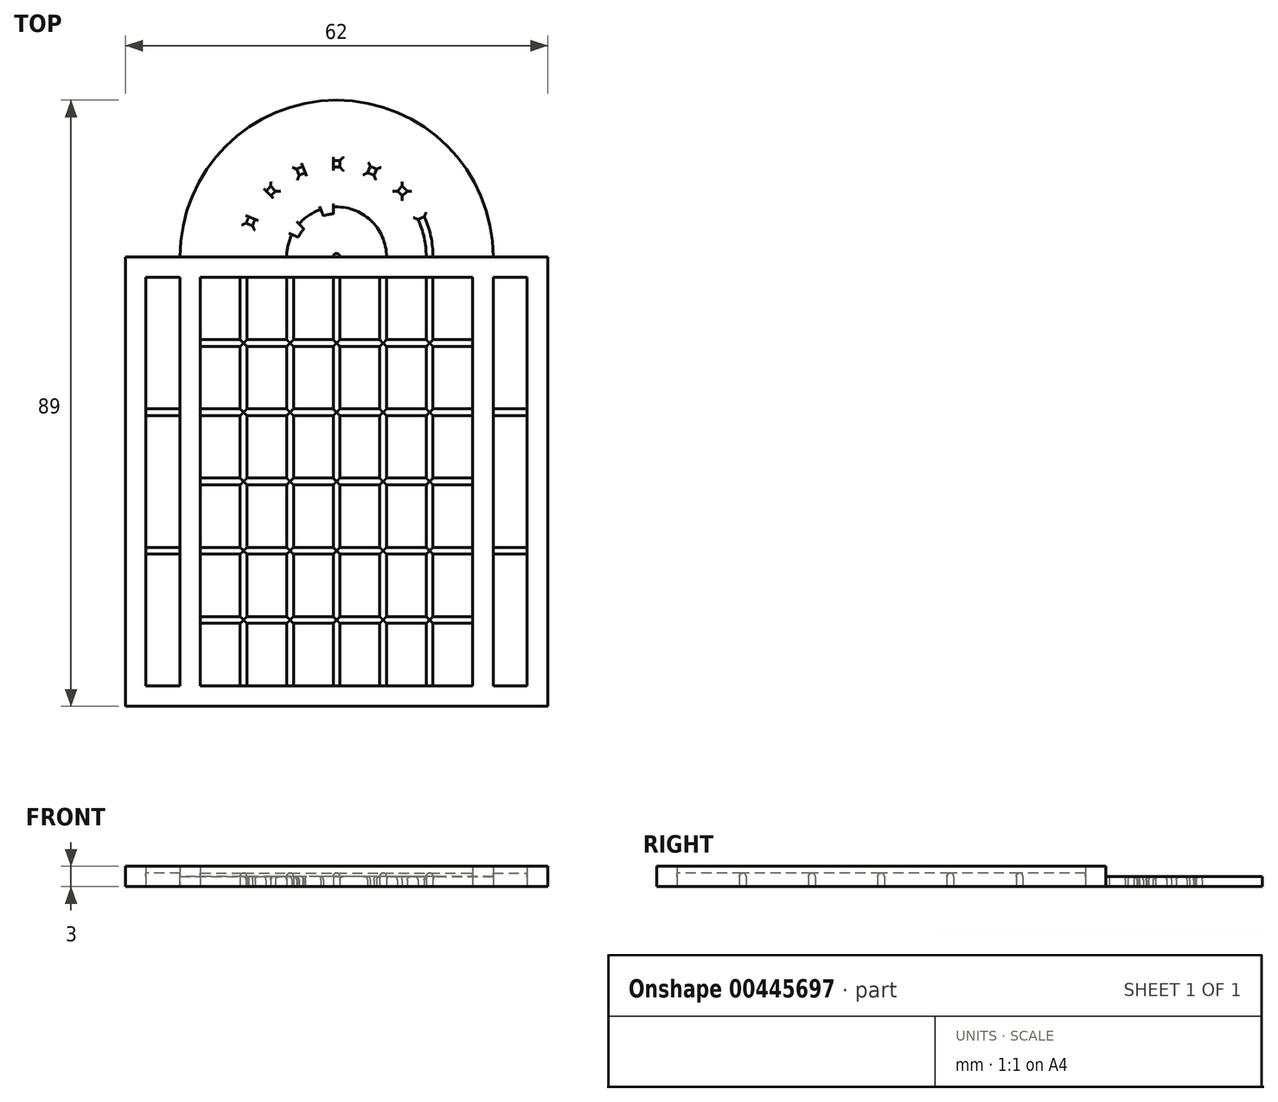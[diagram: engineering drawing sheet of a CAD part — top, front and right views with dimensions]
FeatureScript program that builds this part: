
annotation { "Feature Type Name" : "Feature", "Feature Type Description" : "" }
export const myFeature = defineFeature(function(context is Context, id is Id, definition is map)
    precondition{}
    {
        {
            var Q0;
            Q0=qCreatedBy(makeId("Top.planeOp"),FACE);
            var sketch = newSketch(context, id + "F0", { "sketchPlane" : qUnion([Q0])});
            skLineSegment(sketch, "E0.bottom", {"start": v(0, 0) * mm, "end": v(62, 0) * mm});
            skLineSegment(sketch, "E0.top", {"start": v(0, 60) * mm, "end": v(62, 60) * mm});
            skLineSegment(sketch, "E0.left", {"start": v(0, 0) * mm, "end": v(0, 60) * mm});
            skLineSegment(sketch, "E0.right", {"start": v(62, 0) * mm, "end": v(62, 60) * mm});
            skLineSegment(sketch, "E1", {"start": v(0, 0) * mm, "end": v(8, 0) * mm, "construction": true});
            skLineSegment(sketch, "E2", {"start": v(62, 0) * mm, "end": v(54, 0) * mm, "construction": true});
            skLineSegment(sketch, "E3", {"start": v(62, 0) * mm, "end": v(59, 0) * mm, "construction": true});
            skLineSegment(sketch, "E4", {"start": v(59, 0) * mm, "end": v(59, 60) * mm});
            skLineSegment(sketch, "E5", {"start": v(0, 60) * mm, "end": v(3, 60) * mm, "construction": true});
            skLineSegment(sketch, "E6", {"start": v(3, 60) * mm, "end": v(3, 0) * mm});
            skLineSegment(sketch, "E7", {"start": v(8, 0) * mm, "end": v(8, 60) * mm});
            skLineSegment(sketch, "E8", {"start": v(54, 0) * mm, "end": v(54, 60) * mm});
            skLineSegment(sketch, "E9", {"start": v(8, 0) * mm, "end": v(11, 0) * mm, "construction": true});
            skLineSegment(sketch, "E10", {"start": v(54, 0) * mm, "end": v(51, 0) * mm, "construction": true});
            skLineSegment(sketch, "E11", {"start": v(11, 0) * mm, "end": v(11, 60) * mm});
            skLineSegment(sketch, "E12", {"start": v(51, 0) * mm, "end": v(51, 60) * mm});
            skLineSegment(sketch, "E13.bottom", {"start": v(51, 0) * mm, "end": v(45.17, 0) * mm});
            skLineSegment(sketch, "E13.top", {"start": v(51, 9.17) * mm, "end": v(45.17, 9.17) * mm});
            skLineSegment(sketch, "E13.left", {"start": v(51, 0) * mm, "end": v(51, 9.17) * mm});
            skLineSegment(sketch, "E13.right", {"start": v(45.17, 0) * mm, "end": v(45.17, 9.17) * mm});
            skLineSegment(sketch, "E14.bottom", {"start": v(45.17, 0) * mm, "end": v(44.17, 0) * mm});
            skLineSegment(sketch, "E14.top", {"start": v(45.17, 9.17) * mm, "end": v(44.17, 9.17) * mm, "construction": true});
            skLineSegment(sketch, "E14.right", {"start": v(44.17, 0) * mm, "end": v(44.17, 9.17) * mm});
            skLineSegment(sketch, "E15.top", {"start": v(51, 10.17) * mm, "end": v(45.17, 10.17) * mm});
            skLineSegment(sketch, "E15.left", {"start": v(51, 9.17) * mm, "end": v(51, 10.17) * mm});
            skLineSegment(sketch, "E15.right", {"start": v(45.17, 9.17) * mm, "end": v(45.17, 10.17) * mm, "construction": true});
            skLineSegment(sketch, "E16", {"start": v(44.17, 9.17) * mm, "end": v(44.17, 10.17) * mm, "construction": true});
            skLineSegment(sketch, "E17", {"start": v(44.17, 10.17) * mm, "end": v(45.17, 10.17) * mm, "construction": true});
            skLineSegment(sketch, "E18.0.1.0", {"start": v(44.17, 20.33) * mm, "end": v(45.17, 20.33) * mm, "construction": true});
            skLineSegment(sketch, "E18.0.1.1", {"start": v(51, 20.33) * mm, "end": v(45.17, 20.33) * mm});
            skLineSegment(sketch, "E18.0.1.2", {"start": v(51, 19.33) * mm, "end": v(45.17, 19.33) * mm});
            skLineSegment(sketch, "E18.0.1.3", {"start": v(45.17, 10.17) * mm, "end": v(45.17, 19.33) * mm});
            skLineSegment(sketch, "E18.0.1.4", {"start": v(44.17, 10.17) * mm, "end": v(44.17, 19.33) * mm});
            skLineSegment(sketch, "E18.0.1.5", {"start": v(45.17, 19.33) * mm, "end": v(44.17, 19.33) * mm, "construction": true});
            skLineSegment(sketch, "E18.0.1.6", {"start": v(44.17, 19.33) * mm, "end": v(44.17, 20.33) * mm, "construction": true});
            skLineSegment(sketch, "E18.0.1.7", {"start": v(45.17, 19.33) * mm, "end": v(45.17, 20.33) * mm, "construction": true});
            skLineSegment(sketch, "E18.0.2.0", {"start": v(44.17, 30.5) * mm, "end": v(45.17, 30.5) * mm, "construction": true});
            skLineSegment(sketch, "E18.0.2.1", {"start": v(51, 30.5) * mm, "end": v(45.17, 30.5) * mm});
            skLineSegment(sketch, "E18.0.2.2", {"start": v(51, 29.5) * mm, "end": v(45.17, 29.5) * mm});
            skLineSegment(sketch, "E18.0.2.3", {"start": v(45.17, 20.33) * mm, "end": v(45.17, 29.5) * mm});
            skLineSegment(sketch, "E18.0.2.4", {"start": v(44.17, 20.33) * mm, "end": v(44.17, 29.5) * mm});
            skLineSegment(sketch, "E18.0.2.5", {"start": v(45.17, 29.5) * mm, "end": v(44.17, 29.5) * mm, "construction": true});
            skLineSegment(sketch, "E18.0.2.6", {"start": v(44.17, 29.5) * mm, "end": v(44.17, 30.5) * mm, "construction": true});
            skLineSegment(sketch, "E18.0.2.7", {"start": v(45.17, 29.5) * mm, "end": v(45.17, 30.5) * mm, "construction": true});
            skLineSegment(sketch, "E18.0.3.0", {"start": v(44.17, 40.67) * mm, "end": v(45.17, 40.67) * mm, "construction": true});
            skLineSegment(sketch, "E18.0.3.1", {"start": v(51, 40.67) * mm, "end": v(45.17, 40.67) * mm});
            skLineSegment(sketch, "E18.0.3.2", {"start": v(51, 39.67) * mm, "end": v(45.17, 39.67) * mm});
            skLineSegment(sketch, "E18.0.3.3", {"start": v(45.17, 30.5) * mm, "end": v(45.17, 39.67) * mm});
            skLineSegment(sketch, "E18.0.3.4", {"start": v(44.17, 30.5) * mm, "end": v(44.17, 39.67) * mm});
            skLineSegment(sketch, "E18.0.3.5", {"start": v(45.17, 39.67) * mm, "end": v(44.17, 39.67) * mm, "construction": true});
            skLineSegment(sketch, "E18.0.3.6", {"start": v(44.17, 39.67) * mm, "end": v(44.17, 40.67) * mm, "construction": true});
            skLineSegment(sketch, "E18.0.3.7", {"start": v(45.17, 39.67) * mm, "end": v(45.17, 40.67) * mm, "construction": true});
            skLineSegment(sketch, "E18.0.4.0", {"start": v(44.17, 50.83) * mm, "end": v(45.17, 50.83) * mm, "construction": true});
            skLineSegment(sketch, "E18.0.4.1", {"start": v(51, 50.83) * mm, "end": v(45.17, 50.83) * mm});
            skLineSegment(sketch, "E18.0.4.2", {"start": v(51, 49.83) * mm, "end": v(45.17, 49.83) * mm});
            skLineSegment(sketch, "E18.0.4.3", {"start": v(45.17, 40.67) * mm, "end": v(45.17, 49.83) * mm});
            skLineSegment(sketch, "E18.0.4.4", {"start": v(44.17, 40.67) * mm, "end": v(44.17, 49.83) * mm});
            skLineSegment(sketch, "E18.0.4.5", {"start": v(45.17, 49.83) * mm, "end": v(44.17, 49.83) * mm, "construction": true});
            skLineSegment(sketch, "E18.0.4.6", {"start": v(44.17, 49.83) * mm, "end": v(44.17, 50.83) * mm, "construction": true});
            skLineSegment(sketch, "E18.0.4.7", {"start": v(45.17, 49.83) * mm, "end": v(45.17, 50.83) * mm, "construction": true});
            skLineSegment(sketch, "E18.0.5.2", {"start": v(51, 60) * mm, "end": v(45.17, 60) * mm});
            skLineSegment(sketch, "E18.0.5.3", {"start": v(45.17, 50.83) * mm, "end": v(45.17, 60) * mm});
            skLineSegment(sketch, "E18.0.5.4", {"start": v(44.17, 50.83) * mm, "end": v(44.17, 60) * mm});
            skLineSegment(sketch, "E18.0.5.5", {"start": v(45.17, 60) * mm, "end": v(44.17, 60) * mm, "construction": true});
            skLineSegment(sketch, "E18.1.0.0", {"start": v(37.33, 10.17) * mm, "end": v(38.33, 10.17) * mm, "construction": true});
            skLineSegment(sketch, "E18.1.0.1", {"start": v(44.17, 10.17) * mm, "end": v(38.33, 10.17) * mm});
            skLineSegment(sketch, "E18.1.0.2", {"start": v(44.17, 9.17) * mm, "end": v(38.33, 9.17) * mm});
            skLineSegment(sketch, "E18.1.0.3", {"start": v(38.33, 0) * mm, "end": v(38.33, 9.17) * mm});
            skLineSegment(sketch, "E18.1.0.4", {"start": v(37.33, 0) * mm, "end": v(37.33, 9.17) * mm});
            skLineSegment(sketch, "E18.1.0.5", {"start": v(38.33, 9.17) * mm, "end": v(37.33, 9.17) * mm, "construction": true});
            skLineSegment(sketch, "E18.1.0.6", {"start": v(37.33, 9.17) * mm, "end": v(37.33, 10.17) * mm, "construction": true});
            skLineSegment(sketch, "E18.1.0.7", {"start": v(38.33, 9.17) * mm, "end": v(38.33, 10.17) * mm, "construction": true});
            skLineSegment(sketch, "E18.1.1.0", {"start": v(37.33, 20.33) * mm, "end": v(38.33, 20.33) * mm, "construction": true});
            skLineSegment(sketch, "E18.1.1.1", {"start": v(44.17, 20.33) * mm, "end": v(38.33, 20.33) * mm});
            skLineSegment(sketch, "E18.1.1.2", {"start": v(44.17, 19.33) * mm, "end": v(38.33, 19.33) * mm});
            skLineSegment(sketch, "E18.1.1.3", {"start": v(38.33, 10.17) * mm, "end": v(38.33, 19.33) * mm});
            skLineSegment(sketch, "E18.1.1.4", {"start": v(37.33, 10.17) * mm, "end": v(37.33, 19.33) * mm});
            skLineSegment(sketch, "E18.1.1.5", {"start": v(38.33, 19.33) * mm, "end": v(37.33, 19.33) * mm, "construction": true});
            skLineSegment(sketch, "E18.1.1.6", {"start": v(37.33, 19.33) * mm, "end": v(37.33, 20.33) * mm, "construction": true});
            skLineSegment(sketch, "E18.1.1.7", {"start": v(38.33, 19.33) * mm, "end": v(38.33, 20.33) * mm, "construction": true});
            skLineSegment(sketch, "E18.1.2.0", {"start": v(37.33, 30.5) * mm, "end": v(38.33, 30.5) * mm, "construction": true});
            skLineSegment(sketch, "E18.1.2.1", {"start": v(44.17, 30.5) * mm, "end": v(38.33, 30.5) * mm});
            skLineSegment(sketch, "E18.1.2.2", {"start": v(44.17, 29.5) * mm, "end": v(38.33, 29.5) * mm});
            skLineSegment(sketch, "E18.1.2.3", {"start": v(38.33, 20.33) * mm, "end": v(38.33, 29.5) * mm});
            skLineSegment(sketch, "E18.1.2.4", {"start": v(37.33, 20.33) * mm, "end": v(37.33, 29.5) * mm});
            skLineSegment(sketch, "E18.1.2.5", {"start": v(38.33, 29.5) * mm, "end": v(37.33, 29.5) * mm, "construction": true});
            skLineSegment(sketch, "E18.1.2.6", {"start": v(37.33, 29.5) * mm, "end": v(37.33, 30.5) * mm, "construction": true});
            skLineSegment(sketch, "E18.1.2.7", {"start": v(38.33, 29.5) * mm, "end": v(38.33, 30.5) * mm, "construction": true});
            skLineSegment(sketch, "E18.1.3.0", {"start": v(37.33, 40.67) * mm, "end": v(38.33, 40.67) * mm, "construction": true});
            skLineSegment(sketch, "E18.1.3.1", {"start": v(44.17, 40.67) * mm, "end": v(38.33, 40.67) * mm});
            skLineSegment(sketch, "E18.1.3.2", {"start": v(44.17, 39.67) * mm, "end": v(38.33, 39.67) * mm});
            skLineSegment(sketch, "E18.1.3.3", {"start": v(38.33, 30.5) * mm, "end": v(38.33, 39.67) * mm});
            skLineSegment(sketch, "E18.1.3.4", {"start": v(37.33, 30.5) * mm, "end": v(37.33, 39.67) * mm});
            skLineSegment(sketch, "E18.1.3.5", {"start": v(38.33, 39.67) * mm, "end": v(37.33, 39.67) * mm, "construction": true});
            skLineSegment(sketch, "E18.1.3.6", {"start": v(37.33, 39.67) * mm, "end": v(37.33, 40.67) * mm, "construction": true});
            skLineSegment(sketch, "E18.1.3.7", {"start": v(38.33, 39.67) * mm, "end": v(38.33, 40.67) * mm, "construction": true});
            skLineSegment(sketch, "E18.1.4.0", {"start": v(37.33, 50.83) * mm, "end": v(38.33, 50.83) * mm, "construction": true});
            skLineSegment(sketch, "E18.1.4.1", {"start": v(44.17, 50.83) * mm, "end": v(38.33, 50.83) * mm});
            skLineSegment(sketch, "E18.1.4.2", {"start": v(44.17, 49.83) * mm, "end": v(38.33, 49.83) * mm});
            skLineSegment(sketch, "E18.1.4.3", {"start": v(38.33, 40.67) * mm, "end": v(38.33, 49.83) * mm});
            skLineSegment(sketch, "E18.1.4.4", {"start": v(37.33, 40.67) * mm, "end": v(37.33, 49.83) * mm});
            skLineSegment(sketch, "E18.1.4.5", {"start": v(38.33, 49.83) * mm, "end": v(37.33, 49.83) * mm, "construction": true});
            skLineSegment(sketch, "E18.1.4.6", {"start": v(37.33, 49.83) * mm, "end": v(37.33, 50.83) * mm, "construction": true});
            skLineSegment(sketch, "E18.1.4.7", {"start": v(38.33, 49.83) * mm, "end": v(38.33, 50.83) * mm, "construction": true});
            skLineSegment(sketch, "E18.1.5.2", {"start": v(44.17, 60) * mm, "end": v(38.33, 60) * mm});
            skLineSegment(sketch, "E18.1.5.3", {"start": v(38.33, 50.83) * mm, "end": v(38.33, 60) * mm});
            skLineSegment(sketch, "E18.1.5.4", {"start": v(37.33, 50.83) * mm, "end": v(37.33, 60) * mm});
            skLineSegment(sketch, "E18.1.5.5", {"start": v(38.33, 60) * mm, "end": v(37.33, 60) * mm, "construction": true});
            skLineSegment(sketch, "E18.2.0.0", {"start": v(30.5, 10.17) * mm, "end": v(31.5, 10.17) * mm, "construction": true});
            skLineSegment(sketch, "E18.2.0.1", {"start": v(37.33, 10.17) * mm, "end": v(31.5, 10.17) * mm});
            skLineSegment(sketch, "E18.2.0.2", {"start": v(37.33, 9.17) * mm, "end": v(31.5, 9.17) * mm});
            skLineSegment(sketch, "E18.2.0.3", {"start": v(31.5, 0) * mm, "end": v(31.5, 9.17) * mm});
            skLineSegment(sketch, "E18.2.0.4", {"start": v(30.5, 0) * mm, "end": v(30.5, 9.17) * mm});
            skLineSegment(sketch, "E18.2.0.5", {"start": v(31.5, 9.17) * mm, "end": v(30.5, 9.17) * mm, "construction": true});
            skLineSegment(sketch, "E18.2.0.6", {"start": v(30.5, 9.17) * mm, "end": v(30.5, 10.17) * mm, "construction": true});
            skLineSegment(sketch, "E18.2.0.7", {"start": v(31.5, 9.17) * mm, "end": v(31.5, 10.17) * mm, "construction": true});
            skLineSegment(sketch, "E18.2.1.0", {"start": v(30.5, 20.33) * mm, "end": v(31.5, 20.33) * mm, "construction": true});
            skLineSegment(sketch, "E18.2.1.1", {"start": v(37.33, 20.33) * mm, "end": v(31.5, 20.33) * mm});
            skLineSegment(sketch, "E18.2.1.2", {"start": v(37.33, 19.33) * mm, "end": v(31.5, 19.33) * mm});
            skLineSegment(sketch, "E18.2.1.3", {"start": v(31.5, 10.17) * mm, "end": v(31.5, 19.33) * mm});
            skLineSegment(sketch, "E18.2.1.4", {"start": v(30.5, 10.17) * mm, "end": v(30.5, 19.33) * mm});
            skLineSegment(sketch, "E18.2.1.5", {"start": v(31.5, 19.33) * mm, "end": v(30.5, 19.33) * mm, "construction": true});
            skLineSegment(sketch, "E18.2.1.6", {"start": v(30.5, 19.33) * mm, "end": v(30.5, 20.33) * mm, "construction": true});
            skLineSegment(sketch, "E18.2.1.7", {"start": v(31.5, 19.33) * mm, "end": v(31.5, 20.33) * mm, "construction": true});
            skLineSegment(sketch, "E18.2.2.0", {"start": v(30.5, 30.5) * mm, "end": v(31.5, 30.5) * mm, "construction": true});
            skLineSegment(sketch, "E18.2.2.1", {"start": v(37.33, 30.5) * mm, "end": v(31.5, 30.5) * mm});
            skLineSegment(sketch, "E18.2.2.2", {"start": v(37.33, 29.5) * mm, "end": v(31.5, 29.5) * mm});
            skLineSegment(sketch, "E18.2.2.3", {"start": v(31.5, 20.33) * mm, "end": v(31.5, 29.5) * mm});
            skLineSegment(sketch, "E18.2.2.4", {"start": v(30.5, 20.33) * mm, "end": v(30.5, 29.5) * mm});
            skLineSegment(sketch, "E18.2.2.5", {"start": v(31.5, 29.5) * mm, "end": v(30.5, 29.5) * mm, "construction": true});
            skLineSegment(sketch, "E18.2.2.6", {"start": v(30.5, 29.5) * mm, "end": v(30.5, 30.5) * mm, "construction": true});
            skLineSegment(sketch, "E18.2.2.7", {"start": v(31.5, 29.5) * mm, "end": v(31.5, 30.5) * mm, "construction": true});
            skLineSegment(sketch, "E18.2.3.0", {"start": v(30.5, 40.67) * mm, "end": v(31.5, 40.67) * mm, "construction": true});
            skLineSegment(sketch, "E18.2.3.1", {"start": v(37.33, 40.67) * mm, "end": v(31.5, 40.67) * mm});
            skLineSegment(sketch, "E18.2.3.2", {"start": v(37.33, 39.67) * mm, "end": v(31.5, 39.67) * mm});
            skLineSegment(sketch, "E18.2.3.3", {"start": v(31.5, 30.5) * mm, "end": v(31.5, 39.67) * mm});
            skLineSegment(sketch, "E18.2.3.4", {"start": v(30.5, 30.5) * mm, "end": v(30.5, 39.67) * mm});
            skLineSegment(sketch, "E18.2.3.5", {"start": v(31.5, 39.67) * mm, "end": v(30.5, 39.67) * mm, "construction": true});
            skLineSegment(sketch, "E18.2.3.6", {"start": v(30.5, 39.67) * mm, "end": v(30.5, 40.67) * mm, "construction": true});
            skLineSegment(sketch, "E18.2.3.7", {"start": v(31.5, 39.67) * mm, "end": v(31.5, 40.67) * mm, "construction": true});
            skLineSegment(sketch, "E18.2.4.0", {"start": v(30.5, 50.83) * mm, "end": v(31.5, 50.83) * mm, "construction": true});
            skLineSegment(sketch, "E18.2.4.1", {"start": v(37.33, 50.83) * mm, "end": v(31.5, 50.83) * mm});
            skLineSegment(sketch, "E18.2.4.2", {"start": v(37.33, 49.83) * mm, "end": v(31.5, 49.83) * mm});
            skLineSegment(sketch, "E18.2.4.3", {"start": v(31.5, 40.67) * mm, "end": v(31.5, 49.83) * mm});
            skLineSegment(sketch, "E18.2.4.4", {"start": v(30.5, 40.67) * mm, "end": v(30.5, 49.83) * mm});
            skLineSegment(sketch, "E18.2.4.5", {"start": v(31.5, 49.83) * mm, "end": v(30.5, 49.83) * mm, "construction": true});
            skLineSegment(sketch, "E18.2.4.6", {"start": v(30.5, 49.83) * mm, "end": v(30.5, 50.83) * mm, "construction": true});
            skLineSegment(sketch, "E18.2.4.7", {"start": v(31.5, 49.83) * mm, "end": v(31.5, 50.83) * mm, "construction": true});
            skLineSegment(sketch, "E18.2.5.2", {"start": v(37.33, 60) * mm, "end": v(31.5, 60) * mm});
            skLineSegment(sketch, "E18.2.5.3", {"start": v(31.5, 50.83) * mm, "end": v(31.5, 60) * mm});
            skLineSegment(sketch, "E18.2.5.4", {"start": v(30.5, 50.83) * mm, "end": v(30.5, 60) * mm});
            skLineSegment(sketch, "E18.2.5.5", {"start": v(31.5, 60) * mm, "end": v(30.5, 60) * mm, "construction": true});
            skLineSegment(sketch, "E18.3.0.0", {"start": v(23.67, 10.17) * mm, "end": v(24.67, 10.17) * mm, "construction": true});
            skLineSegment(sketch, "E18.3.0.1", {"start": v(30.5, 10.17) * mm, "end": v(24.67, 10.17) * mm});
            skLineSegment(sketch, "E18.3.0.2", {"start": v(30.5, 9.17) * mm, "end": v(24.67, 9.17) * mm});
            skLineSegment(sketch, "E18.3.0.3", {"start": v(24.67, 0) * mm, "end": v(24.67, 9.17) * mm});
            skLineSegment(sketch, "E18.3.0.4", {"start": v(23.67, 0) * mm, "end": v(23.67, 9.17) * mm});
            skLineSegment(sketch, "E18.3.0.5", {"start": v(24.67, 9.17) * mm, "end": v(23.67, 9.17) * mm, "construction": true});
            skLineSegment(sketch, "E18.3.0.6", {"start": v(23.67, 9.17) * mm, "end": v(23.67, 10.17) * mm, "construction": true});
            skLineSegment(sketch, "E18.3.0.7", {"start": v(24.67, 9.17) * mm, "end": v(24.67, 10.17) * mm, "construction": true});
            skLineSegment(sketch, "E18.3.1.0", {"start": v(23.67, 20.33) * mm, "end": v(24.67, 20.33) * mm, "construction": true});
            skLineSegment(sketch, "E18.3.1.1", {"start": v(30.5, 20.33) * mm, "end": v(24.67, 20.33) * mm});
            skLineSegment(sketch, "E18.3.1.2", {"start": v(30.5, 19.33) * mm, "end": v(24.67, 19.33) * mm});
            skLineSegment(sketch, "E18.3.1.3", {"start": v(24.67, 10.17) * mm, "end": v(24.67, 19.33) * mm});
            skLineSegment(sketch, "E18.3.1.4", {"start": v(23.67, 10.17) * mm, "end": v(23.67, 19.33) * mm});
            skLineSegment(sketch, "E18.3.1.5", {"start": v(24.67, 19.33) * mm, "end": v(23.67, 19.33) * mm, "construction": true});
            skLineSegment(sketch, "E18.3.1.6", {"start": v(23.67, 19.33) * mm, "end": v(23.67, 20.33) * mm, "construction": true});
            skLineSegment(sketch, "E18.3.1.7", {"start": v(24.67, 19.33) * mm, "end": v(24.67, 20.33) * mm, "construction": true});
            skLineSegment(sketch, "E18.3.2.0", {"start": v(23.67, 30.5) * mm, "end": v(24.67, 30.5) * mm, "construction": true});
            skLineSegment(sketch, "E18.3.2.1", {"start": v(30.5, 30.5) * mm, "end": v(24.67, 30.5) * mm});
            skLineSegment(sketch, "E18.3.2.2", {"start": v(30.5, 29.5) * mm, "end": v(24.67, 29.5) * mm});
            skLineSegment(sketch, "E18.3.2.3", {"start": v(24.67, 20.33) * mm, "end": v(24.67, 29.5) * mm});
            skLineSegment(sketch, "E18.3.2.4", {"start": v(23.67, 20.33) * mm, "end": v(23.67, 29.5) * mm});
            skLineSegment(sketch, "E18.3.2.5", {"start": v(24.67, 29.5) * mm, "end": v(23.67, 29.5) * mm, "construction": true});
            skLineSegment(sketch, "E18.3.2.6", {"start": v(23.67, 29.5) * mm, "end": v(23.67, 30.5) * mm, "construction": true});
            skLineSegment(sketch, "E18.3.2.7", {"start": v(24.67, 29.5) * mm, "end": v(24.67, 30.5) * mm, "construction": true});
            skLineSegment(sketch, "E18.3.3.0", {"start": v(23.67, 40.67) * mm, "end": v(24.67, 40.67) * mm, "construction": true});
            skLineSegment(sketch, "E18.3.3.1", {"start": v(30.5, 40.67) * mm, "end": v(24.67, 40.67) * mm});
            skLineSegment(sketch, "E18.3.3.2", {"start": v(30.5, 39.67) * mm, "end": v(24.67, 39.67) * mm});
            skLineSegment(sketch, "E18.3.3.3", {"start": v(24.67, 30.5) * mm, "end": v(24.67, 39.67) * mm});
            skLineSegment(sketch, "E18.3.3.4", {"start": v(23.67, 30.5) * mm, "end": v(23.67, 39.67) * mm});
            skLineSegment(sketch, "E18.3.3.5", {"start": v(24.67, 39.67) * mm, "end": v(23.67, 39.67) * mm, "construction": true});
            skLineSegment(sketch, "E18.3.3.6", {"start": v(23.67, 39.67) * mm, "end": v(23.67, 40.67) * mm, "construction": true});
            skLineSegment(sketch, "E18.3.3.7", {"start": v(24.67, 39.67) * mm, "end": v(24.67, 40.67) * mm, "construction": true});
            skLineSegment(sketch, "E18.3.4.0", {"start": v(23.67, 50.83) * mm, "end": v(24.67, 50.83) * mm, "construction": true});
            skLineSegment(sketch, "E18.3.4.1", {"start": v(30.5, 50.83) * mm, "end": v(24.67, 50.83) * mm});
            skLineSegment(sketch, "E18.3.4.2", {"start": v(30.5, 49.83) * mm, "end": v(24.67, 49.83) * mm});
            skLineSegment(sketch, "E18.3.4.3", {"start": v(24.67, 40.67) * mm, "end": v(24.67, 49.83) * mm});
            skLineSegment(sketch, "E18.3.4.4", {"start": v(23.67, 40.67) * mm, "end": v(23.67, 49.83) * mm});
            skLineSegment(sketch, "E18.3.4.5", {"start": v(24.67, 49.83) * mm, "end": v(23.67, 49.83) * mm, "construction": true});
            skLineSegment(sketch, "E18.3.4.6", {"start": v(23.67, 49.83) * mm, "end": v(23.67, 50.83) * mm, "construction": true});
            skLineSegment(sketch, "E18.3.4.7", {"start": v(24.67, 49.83) * mm, "end": v(24.67, 50.83) * mm, "construction": true});
            skLineSegment(sketch, "E18.3.5.2", {"start": v(30.5, 60) * mm, "end": v(24.67, 60) * mm});
            skLineSegment(sketch, "E18.3.5.3", {"start": v(24.67, 50.83) * mm, "end": v(24.67, 60) * mm});
            skLineSegment(sketch, "E18.3.5.4", {"start": v(23.67, 50.83) * mm, "end": v(23.67, 60) * mm});
            skLineSegment(sketch, "E18.3.5.5", {"start": v(24.67, 60) * mm, "end": v(23.67, 60) * mm, "construction": true});
            skLineSegment(sketch, "E18.4.0.0", {"start": v(16.83, 10.17) * mm, "end": v(17.83, 10.17) * mm, "construction": true});
            skLineSegment(sketch, "E18.4.0.1", {"start": v(23.67, 10.17) * mm, "end": v(17.83, 10.17) * mm});
            skLineSegment(sketch, "E18.4.0.2", {"start": v(23.67, 9.17) * mm, "end": v(17.83, 9.17) * mm});
            skLineSegment(sketch, "E18.4.0.3", {"start": v(17.83, 0) * mm, "end": v(17.83, 9.17) * mm});
            skLineSegment(sketch, "E18.4.0.4", {"start": v(16.83, 0) * mm, "end": v(16.83, 9.17) * mm});
            skLineSegment(sketch, "E18.4.0.5", {"start": v(17.83, 9.17) * mm, "end": v(16.83, 9.17) * mm, "construction": true});
            skLineSegment(sketch, "E18.4.0.6", {"start": v(16.83, 9.17) * mm, "end": v(16.83, 10.17) * mm, "construction": true});
            skLineSegment(sketch, "E18.4.0.7", {"start": v(17.83, 9.17) * mm, "end": v(17.83, 10.17) * mm, "construction": true});
            skLineSegment(sketch, "E18.4.1.0", {"start": v(16.83, 20.33) * mm, "end": v(17.83, 20.33) * mm, "construction": true});
            skLineSegment(sketch, "E18.4.1.1", {"start": v(23.67, 20.33) * mm, "end": v(17.83, 20.33) * mm});
            skLineSegment(sketch, "E18.4.1.2", {"start": v(23.67, 19.33) * mm, "end": v(17.83, 19.33) * mm});
            skLineSegment(sketch, "E18.4.1.3", {"start": v(17.83, 10.17) * mm, "end": v(17.83, 19.33) * mm});
            skLineSegment(sketch, "E18.4.1.4", {"start": v(16.83, 10.17) * mm, "end": v(16.83, 19.33) * mm});
            skLineSegment(sketch, "E18.4.1.5", {"start": v(17.83, 19.33) * mm, "end": v(16.83, 19.33) * mm, "construction": true});
            skLineSegment(sketch, "E18.4.1.6", {"start": v(16.83, 19.33) * mm, "end": v(16.83, 20.33) * mm, "construction": true});
            skLineSegment(sketch, "E18.4.1.7", {"start": v(17.83, 19.33) * mm, "end": v(17.83, 20.33) * mm, "construction": true});
            skLineSegment(sketch, "E18.4.2.0", {"start": v(16.83, 30.5) * mm, "end": v(17.83, 30.5) * mm, "construction": true});
            skLineSegment(sketch, "E18.4.2.1", {"start": v(23.67, 30.5) * mm, "end": v(17.83, 30.5) * mm});
            skLineSegment(sketch, "E18.4.2.2", {"start": v(23.67, 29.5) * mm, "end": v(17.83, 29.5) * mm});
            skLineSegment(sketch, "E18.4.2.3", {"start": v(17.83, 20.33) * mm, "end": v(17.83, 29.5) * mm});
            skLineSegment(sketch, "E18.4.2.4", {"start": v(16.83, 20.33) * mm, "end": v(16.83, 29.5) * mm});
            skLineSegment(sketch, "E18.4.2.5", {"start": v(17.83, 29.5) * mm, "end": v(16.83, 29.5) * mm, "construction": true});
            skLineSegment(sketch, "E18.4.2.6", {"start": v(16.83, 29.5) * mm, "end": v(16.83, 30.5) * mm, "construction": true});
            skLineSegment(sketch, "E18.4.2.7", {"start": v(17.83, 29.5) * mm, "end": v(17.83, 30.5) * mm, "construction": true});
            skLineSegment(sketch, "E18.4.3.0", {"start": v(16.83, 40.67) * mm, "end": v(17.83, 40.67) * mm, "construction": true});
            skLineSegment(sketch, "E18.4.3.1", {"start": v(23.67, 40.67) * mm, "end": v(17.83, 40.67) * mm});
            skLineSegment(sketch, "E18.4.3.2", {"start": v(23.67, 39.67) * mm, "end": v(17.83, 39.67) * mm});
            skLineSegment(sketch, "E18.4.3.3", {"start": v(17.83, 30.5) * mm, "end": v(17.83, 39.67) * mm});
            skLineSegment(sketch, "E18.4.3.4", {"start": v(16.83, 30.5) * mm, "end": v(16.83, 39.67) * mm});
            skLineSegment(sketch, "E18.4.3.5", {"start": v(17.83, 39.67) * mm, "end": v(16.83, 39.67) * mm, "construction": true});
            skLineSegment(sketch, "E18.4.3.6", {"start": v(16.83, 39.67) * mm, "end": v(16.83, 40.67) * mm, "construction": true});
            skLineSegment(sketch, "E18.4.3.7", {"start": v(17.83, 39.67) * mm, "end": v(17.83, 40.67) * mm, "construction": true});
            skLineSegment(sketch, "E18.4.4.0", {"start": v(16.83, 50.83) * mm, "end": v(17.83, 50.83) * mm, "construction": true});
            skLineSegment(sketch, "E18.4.4.1", {"start": v(23.67, 50.83) * mm, "end": v(17.83, 50.83) * mm});
            skLineSegment(sketch, "E18.4.4.2", {"start": v(23.67, 49.83) * mm, "end": v(17.83, 49.83) * mm});
            skLineSegment(sketch, "E18.4.4.3", {"start": v(17.83, 40.67) * mm, "end": v(17.83, 49.83) * mm});
            skLineSegment(sketch, "E18.4.4.4", {"start": v(16.83, 40.67) * mm, "end": v(16.83, 49.83) * mm});
            skLineSegment(sketch, "E18.4.4.5", {"start": v(17.83, 49.83) * mm, "end": v(16.83, 49.83) * mm, "construction": true});
            skLineSegment(sketch, "E18.4.4.6", {"start": v(16.83, 49.83) * mm, "end": v(16.83, 50.83) * mm, "construction": true});
            skLineSegment(sketch, "E18.4.4.7", {"start": v(17.83, 49.83) * mm, "end": v(17.83, 50.83) * mm, "construction": true});
            skLineSegment(sketch, "E18.4.5.2", {"start": v(23.67, 60) * mm, "end": v(17.83, 60) * mm});
            skLineSegment(sketch, "E18.4.5.3", {"start": v(17.83, 50.83) * mm, "end": v(17.83, 60) * mm});
            skLineSegment(sketch, "E18.4.5.4", {"start": v(16.83, 50.83) * mm, "end": v(16.83, 60) * mm});
            skLineSegment(sketch, "E18.4.5.5", {"start": v(17.83, 60) * mm, "end": v(16.83, 60) * mm, "construction": true});
            skLineSegment(sketch, "E18.5.0.1", {"start": v(16.83, 10.17) * mm, "end": v(11, 10.17) * mm});
            skLineSegment(sketch, "E18.5.0.2", {"start": v(16.83, 9.17) * mm, "end": v(11, 9.17) * mm});
            skLineSegment(sketch, "E18.5.0.3", {"start": v(11, 0) * mm, "end": v(11, 9.17) * mm});
            skLineSegment(sketch, "E18.5.0.7", {"start": v(11, 9.17) * mm, "end": v(11, 10.17) * mm, "construction": true});
            skLineSegment(sketch, "E18.5.1.1", {"start": v(16.83, 20.33) * mm, "end": v(11, 20.33) * mm});
            skLineSegment(sketch, "E18.5.1.2", {"start": v(16.83, 19.33) * mm, "end": v(11, 19.33) * mm});
            skLineSegment(sketch, "E18.5.1.3", {"start": v(11, 10.17) * mm, "end": v(11, 19.33) * mm});
            skLineSegment(sketch, "E18.5.1.7", {"start": v(11, 19.33) * mm, "end": v(11, 20.33) * mm, "construction": true});
            skLineSegment(sketch, "E18.5.2.1", {"start": v(16.83, 30.5) * mm, "end": v(11, 30.5) * mm});
            skLineSegment(sketch, "E18.5.2.2", {"start": v(16.83, 29.5) * mm, "end": v(11, 29.5) * mm});
            skLineSegment(sketch, "E18.5.2.3", {"start": v(11, 20.33) * mm, "end": v(11, 29.5) * mm});
            skLineSegment(sketch, "E18.5.2.7", {"start": v(11, 29.5) * mm, "end": v(11, 30.5) * mm, "construction": true});
            skLineSegment(sketch, "E18.5.3.1", {"start": v(16.83, 40.67) * mm, "end": v(11, 40.67) * mm});
            skLineSegment(sketch, "E18.5.3.2", {"start": v(16.83, 39.67) * mm, "end": v(11, 39.67) * mm});
            skLineSegment(sketch, "E18.5.3.3", {"start": v(11, 30.5) * mm, "end": v(11, 39.67) * mm});
            skLineSegment(sketch, "E18.5.3.7", {"start": v(11, 39.67) * mm, "end": v(11, 40.67) * mm, "construction": true});
            skLineSegment(sketch, "E18.5.4.1", {"start": v(16.83, 50.83) * mm, "end": v(11, 50.83) * mm});
            skLineSegment(sketch, "E18.5.4.2", {"start": v(16.83, 49.83) * mm, "end": v(11, 49.83) * mm});
            skLineSegment(sketch, "E18.5.4.3", {"start": v(11, 40.67) * mm, "end": v(11, 49.83) * mm});
            skLineSegment(sketch, "E18.5.4.7", {"start": v(11, 49.83) * mm, "end": v(11, 50.83) * mm, "construction": true});
            skLineSegment(sketch, "E18.5.5.2", {"start": v(16.83, 60) * mm, "end": v(11, 60) * mm});
            skLineSegment(sketch, "E18.5.5.3", {"start": v(11, 50.83) * mm, "end": v(11, 60) * mm});
            skLineSegment(sketch, "E18.direction1", {"start": v(44.17, 0) * mm, "end": v(37.33, 0) * mm, "construction": true});
            skLineSegment(sketch, "E18.direction2", {"start": v(44.17, 0) * mm, "end": v(44.17, 10.17) * mm, "construction": true});
            skLineSegment(sketch, "E19.top", {"start": v(0, -3) * mm, "end": v(62, -3) * mm});
            skLineSegment(sketch, "E19.left", {"start": v(0, 0) * mm, "end": v(0, -3) * mm});
            skLineSegment(sketch, "E19.right", {"start": v(62, 0) * mm, "end": v(62, -3) * mm});
            skLineSegment(sketch, "E20.top", {"start": v(0, 63) * mm, "end": v(62, 63) * mm});
            skLineSegment(sketch, "E20.left", {"start": v(0, 60) * mm, "end": v(0, 63) * mm});
            skLineSegment(sketch, "E20.right", {"start": v(62, 60) * mm, "end": v(62, 63) * mm});
            skLineSegment(sketch, "E21", {"start": v(31, 63) * mm, "end": v(31, 86) * mm, "construction": true});
            skArc(sketch, "E22", {"start": v(11, 63) * mm, "mid": v(31, 83) * mm, "end": v(51, 63) * mm});
            skArc(sketch, "E23", {"start": v(8, 63) * mm, "mid": v(31, 86) * mm, "end": v(54, 63) * mm});
            skArc(sketch, "E24", {"start": v(16.83, 63) * mm, "mid": v(31, 77.17) * mm, "end": v(45.17, 63) * mm});
            skArc(sketch, "E25", {"start": v(17.83, 63) * mm, "mid": v(31, 76.17) * mm, "end": v(44.17, 63) * mm});
            skArc(sketch, "E26", {"start": v(23.67, 63) * mm, "mid": v(31, 70.33) * mm, "end": v(38.33, 63) * mm});
            skArc(sketch, "E27", {"start": v(24.67, 63) * mm, "mid": v(31, 69.33) * mm, "end": v(37.33, 63) * mm});
            skArc(sketch, "E28", {"start": v(30.5, 63) * mm, "mid": v(31, 63.5) * mm, "end": v(31.5, 63) * mm});
            skLineSegment(sketch, "E29", {"start": v(31, 63) * mm, "end": v(8, 63) * mm});
            skLineSegment(sketch, "E30.1.0", {"start": v(31, 63) * mm, "end": v(9.75, 71.8) * mm, "construction": true});
            skLineSegment(sketch, "E30.2.0", {"start": v(31, 63) * mm, "end": v(14.74, 79.26) * mm, "construction": true});
            skLineSegment(sketch, "E30.3.0", {"start": v(31, 63) * mm, "end": v(22.2, 84.25) * mm, "construction": true});
            skLineSegment(sketch, "E30.5.0", {"start": v(31, 63) * mm, "end": v(39.8, 84.25) * mm, "construction": true});
            skLineSegment(sketch, "E30.6.0", {"start": v(31, 63) * mm, "end": v(47.26, 79.26) * mm, "construction": true});
            skLineSegment(sketch, "E30.7.0", {"start": v(31, 63) * mm, "end": v(52.25, 71.8) * mm, "construction": true});
            skLineSegment(sketch, "E30.8.0", {"start": v(31, 63) * mm, "end": v(54, 63) * mm});
            skLineSegment(sketch, "E30.anchor1", {"start": v(31, 63) * mm, "end": v(8, 63) * mm, "construction": true});
            skLineSegment(sketch, "E30.anchor2", {"start": v(31, 63) * mm, "end": v(54, 63) * mm, "construction": true});
            skLineSegment(sketch, "E31.0", {"start": v(30.08, 63.92) * mm, "end": v(12.72, 71.11) * mm});
            skLineSegment(sketch, "E32.MirrorCS", {"start": v(29.7, 63) * mm, "end": v(12.34, 70.19) * mm});
            skLineSegment(sketch, "E33.0", {"start": v(30.5, 64.2) * mm, "end": v(17.22, 77.5) * mm});
            skLineSegment(sketch, "E34.MirrorCS", {"start": v(28.87, 64.42) * mm, "end": v(16.5, 76.78) * mm});
            skLineSegment(sketch, "E35.0", {"start": v(31, 64.3) * mm, "end": v(23.81, 81.66) * mm});
            skLineSegment(sketch, "E36.MirrorCS", {"start": v(30.08, 63.92) * mm, "end": v(22.89, 81.28) * mm});
            skLineSegment(sketch, "E37.0", {"start": v(31.5, 65.51) * mm, "end": v(31.5, 83) * mm});
            skLineSegment(sketch, "E38.0", {"start": v(30.5, 65.51) * mm, "end": v(30.5, 83) * mm});
            skLineSegment(sketch, "E39.0", {"start": v(32.42, 65.13) * mm, "end": v(39.11, 81.28) * mm});
            skLineSegment(sketch, "E40.0", {"start": v(31, 64.3) * mm, "end": v(38.19, 81.66) * mm});
            skLineSegment(sketch, "E41.0", {"start": v(32.3, 63) * mm, "end": v(49.66, 70.19) * mm});
            skLineSegment(sketch, "E42.0", {"start": v(33.13, 64.42) * mm, "end": v(49.28, 71.11) * mm});
            skLineSegment(sketch, "E43.0", {"start": v(33.13, 64.42) * mm, "end": v(45.5, 76.78) * mm});
            skLineSegment(sketch, "E44.0", {"start": v(32.42, 65.13) * mm, "end": v(44.78, 77.5) * mm});
            skSolve(sketch);
        }
        {
            var Q0;
            {var subQ13=sQuery(id+"F0.wireOp",EDGE,"E23");Q0=makeQuery(id+"F0.imprint","IMPRINT",FACE,{"disambiguationData":[TD([[makeQuery(id+"F0.imprint","IMPRINT",EDGE,{"derivedFrom":subQ13}),-1.0]])]});}
            var Q1;
            {var subQ1=sQuery(id+"F0.wireOp",EDGE,"E20.left");Q1=makeQuery(id+"F0.imprint","IMPRINT",FACE,{"disambiguationData":[TD([[makeQuery(id+"F0.imprint","IMPRINT",EDGE,{"derivedFrom":subQ1}),-1.0]])]});}
            var Q2;
            {var subQ0=sQuery(id+"F0.wireOp",EDGE,"E0.right");Q2=makeQuery(id+"F0.imprint","IMPRINT",FACE,{"disambiguationData":[TD([[makeQuery(id+"F0.imprint","IMPRINT",EDGE,{"derivedFrom":subQ0}),1.0]])]});}
            var Q3;
            {var subQ7=sQuery(id+"F0.wireOp",EDGE,"E7");Q3=makeQuery(id+"F0.imprint","IMPRINT",FACE,{"disambiguationData":[TD([[makeQuery(id+"F0.imprint","IMPRINT",EDGE,{"derivedFrom":subQ7}),-1.0]])]});}
            var Q4;
            {var subQ0=sQuery(id+"F0.wireOp",EDGE,"E0.left");Q4=makeQuery(id+"F0.imprint","IMPRINT",FACE,{"disambiguationData":[TD([[makeQuery(id+"F0.imprint","IMPRINT",EDGE,{"derivedFrom":subQ0}),-1.0]])]});}
            var Q5;
            {var subQ9=sQuery(id+"F0.wireOp",EDGE,"E8");Q5=makeQuery(id+"F0.imprint","IMPRINT",FACE,{"disambiguationData":[TD([[makeQuery(id+"F0.imprint","IMPRINT",EDGE,{"derivedFrom":subQ9}),1.0]])]});}
            var Q6;
            Q6=makeQuery(id+"F0.imprint","IMPRINT",FACE,{"disambiguationData":[TD([[makeQuery(id+"F0.imprint","IMPRINT",EDGE,{"derivedFrom":sQuery(id+"F0.wireOp",EDGE,"E19.top")}),1.0]])]});
            extrude(context, id + "F1", {"entities" : qUnion([Q0, Q1, Q2, Q3, Q4, Q5, Q6]), "depth" : 3 * mm});
        }
        {
            var Q0;
            {var subQ0=sQuery(id+"F0.wireOp",EDGE,"E29");var subQ1=sQuery(id+"F0.wireOp",EDGE,"E24");var subQ2=makeQuery(id+"F0.imprint","INTERSECT",VERTEX,{"derivedFrom":[subQ1,subQ0]});Q0=makeQuery(id+"F0.imprint","IMPRINT",FACE,{"disambiguationData":[TD([[makeQuery(id+"F0.imprint","IMPRINT",EDGE,{"disambiguationData":[TD([[subQ2,-1.0]])],"derivedFrom":subQ1}),-1.0]])]});}
            var Q1;
            {var subQ0=sQuery(id+"F0.wireOp",EDGE,"E31.0");var subQ1=sQuery(id+"F0.wireOp",EDGE,"E24");var subQ2=makeQuery(id+"F0.imprint","INTERSECT",VERTEX,{"derivedFrom":[subQ1,subQ0]});Q1=makeQuery(id+"F0.imprint","IMPRINT",FACE,{"disambiguationData":[TD([[makeQuery(id+"F0.imprint","IMPRINT",EDGE,{"disambiguationData":[TD([[subQ2,-1.0]])],"derivedFrom":subQ1}),-1.0]])]});}
            var Q2;
            {var subQ0=sQuery(id+"F0.wireOp",EDGE,"E35.0");var subQ1=sQuery(id+"F0.wireOp",EDGE,"E24");var subQ2=makeQuery(id+"F0.imprint","INTERSECT",VERTEX,{"derivedFrom":[subQ1,subQ0]});Q2=makeQuery(id+"F0.imprint","IMPRINT",FACE,{"disambiguationData":[TD([[makeQuery(id+"F0.imprint","IMPRINT",EDGE,{"disambiguationData":[TD([[subQ2,-1.0]])],"derivedFrom":subQ1}),-1.0]])]});}
            var Q3;
            {var subQ0=sQuery(id+"F0.wireOp",EDGE,"E37.0");var subQ1=sQuery(id+"F0.wireOp",EDGE,"E24");var subQ2=makeQuery(id+"F0.imprint","INTERSECT",VERTEX,{"derivedFrom":[subQ1,subQ0]});Q3=makeQuery(id+"F0.imprint","IMPRINT",FACE,{"disambiguationData":[TD([[makeQuery(id+"F0.imprint","IMPRINT",EDGE,{"disambiguationData":[TD([[subQ2,-1.0]])],"derivedFrom":subQ1}),-1.0]])]});}
            var Q4;
            {var subQ0=sQuery(id+"F0.wireOp",EDGE,"E39.0");var subQ1=sQuery(id+"F0.wireOp",EDGE,"E24");var subQ2=makeQuery(id+"F0.imprint","INTERSECT",VERTEX,{"derivedFrom":[subQ1,subQ0]});Q4=makeQuery(id+"F0.imprint","IMPRINT",FACE,{"disambiguationData":[TD([[makeQuery(id+"F0.imprint","IMPRINT",EDGE,{"disambiguationData":[TD([[subQ2,-1.0]])],"derivedFrom":subQ1}),-1.0]])]});}
            var Q5;
            {var subQ0=sQuery(id+"F0.wireOp",EDGE,"E43.0");var subQ1=sQuery(id+"F0.wireOp",EDGE,"E24");var subQ2=makeQuery(id+"F0.imprint","INTERSECT",VERTEX,{"derivedFrom":[subQ1,subQ0]});Q5=makeQuery(id+"F0.imprint","IMPRINT",FACE,{"disambiguationData":[TD([[makeQuery(id+"F0.imprint","IMPRINT",EDGE,{"disambiguationData":[TD([[subQ2,-1.0]])],"derivedFrom":subQ1}),-1.0]])]});}
            var Q6;
            {var subQ0=sQuery(id+"F0.wireOp",EDGE,"E30.8.0");var subQ1=sQuery(id+"F0.wireOp",EDGE,"E24");var subQ2=makeQuery(id+"F0.imprint","INTERSECT",VERTEX,{"derivedFrom":[subQ1,subQ0]});Q6=makeQuery(id+"F0.imprint","IMPRINT",FACE,{"disambiguationData":[TD([[makeQuery(id+"F0.imprint","IMPRINT",EDGE,{"disambiguationData":[TD([[subQ2,1.0]])],"derivedFrom":subQ1}),-1.0]])]});}
            var Q7;
            {var subQ0=sQuery(id+"F0.wireOp",EDGE,"E33.0");var subQ1=sQuery(id+"F0.wireOp",EDGE,"E22");var subQ2=makeQuery(id+"F0.imprint","INTERSECT",VERTEX,{"derivedFrom":[subQ1,subQ0]});Q7=makeQuery(id+"F0.imprint","IMPRINT",FACE,{"disambiguationData":[TD([[makeQuery(id+"F0.imprint","IMPRINT",EDGE,{"disambiguationData":[TD([[subQ2,1.0]])],"derivedFrom":subQ1}),-1.0]])]});}
            var Q8;
            {var subQ0=sQuery(id+"F0.wireOp",EDGE,"E31.0");var subQ1=sQuery(id+"F0.wireOp",EDGE,"E22");var subQ2=makeQuery(id+"F0.imprint","INTERSECT",VERTEX,{"derivedFrom":[subQ1,subQ0]});Q8=makeQuery(id+"F0.imprint","IMPRINT",FACE,{"disambiguationData":[TD([[makeQuery(id+"F0.imprint","IMPRINT",EDGE,{"disambiguationData":[TD([[subQ2,1.0]])],"derivedFrom":subQ1}),-1.0]])]});}
            var Q9;
            {var subQ0=sQuery(id+"F0.wireOp",EDGE,"E35.0");var subQ1=sQuery(id+"F0.wireOp",EDGE,"E22");var subQ2=makeQuery(id+"F0.imprint","INTERSECT",VERTEX,{"derivedFrom":[subQ1,subQ0]});Q9=makeQuery(id+"F0.imprint","IMPRINT",FACE,{"disambiguationData":[TD([[makeQuery(id+"F0.imprint","IMPRINT",EDGE,{"disambiguationData":[TD([[subQ2,1.0]])],"derivedFrom":subQ1}),-1.0]])]});}
            var Q10;
            {var subQ0=sQuery(id+"F0.wireOp",EDGE,"E37.0");var subQ1=sQuery(id+"F0.wireOp",EDGE,"E22");var subQ2=makeQuery(id+"F0.imprint","INTERSECT",VERTEX,{"derivedFrom":[subQ1,subQ0]});Q10=makeQuery(id+"F0.imprint","IMPRINT",FACE,{"disambiguationData":[TD([[makeQuery(id+"F0.imprint","IMPRINT",EDGE,{"disambiguationData":[TD([[subQ2,1.0]])],"derivedFrom":subQ1}),-1.0]])]});}
            var Q11;
            {var subQ0=sQuery(id+"F0.wireOp",EDGE,"E39.0");var subQ1=sQuery(id+"F0.wireOp",EDGE,"E22");var subQ2=makeQuery(id+"F0.imprint","INTERSECT",VERTEX,{"derivedFrom":[subQ1,subQ0]});Q11=makeQuery(id+"F0.imprint","IMPRINT",FACE,{"disambiguationData":[TD([[makeQuery(id+"F0.imprint","IMPRINT",EDGE,{"disambiguationData":[TD([[subQ2,1.0]])],"derivedFrom":subQ1}),-1.0]])]});}
            var Q12;
            {var subQ0=sQuery(id+"F0.wireOp",EDGE,"E43.0");var subQ1=sQuery(id+"F0.wireOp",EDGE,"E22");var subQ2=makeQuery(id+"F0.imprint","INTERSECT",VERTEX,{"derivedFrom":[subQ1,subQ0]});Q12=makeQuery(id+"F0.imprint","IMPRINT",FACE,{"disambiguationData":[TD([[makeQuery(id+"F0.imprint","IMPRINT",EDGE,{"disambiguationData":[TD([[subQ2,1.0]])],"derivedFrom":subQ1}),-1.0]])]});}
            var Q13;
            {var subQ0=sQuery(id+"F0.wireOp",EDGE,"E41.0");var subQ1=sQuery(id+"F0.wireOp",EDGE,"E22");var subQ2=makeQuery(id+"F0.imprint","INTERSECT",VERTEX,{"derivedFrom":[subQ1,subQ0]});Q13=makeQuery(id+"F0.imprint","IMPRINT",FACE,{"disambiguationData":[TD([[makeQuery(id+"F0.imprint","IMPRINT",EDGE,{"disambiguationData":[TD([[subQ2,1.0]])],"derivedFrom":subQ1}),-1.0]])]});}
            var Q14;
            {var subQ0=sQuery(id+"F0.wireOp",EDGE,"E42.0");var subQ1=sQuery(id+"F0.wireOp",EDGE,"E24");var subQ2=makeQuery(id+"F0.imprint","INTERSECT",VERTEX,{"derivedFrom":[subQ1,subQ0]});Q14=makeQuery(id+"F0.imprint","IMPRINT",FACE,{"disambiguationData":[TD([[makeQuery(id+"F0.imprint","IMPRINT",EDGE,{"disambiguationData":[TD([[subQ2,-1.0]])],"derivedFrom":subQ1}),-1.0]])]});}
            var Q15;
            {var subQ0=sQuery(id+"F0.wireOp",EDGE,"E44.0");var subQ1=sQuery(id+"F0.wireOp",EDGE,"E24");var subQ2=makeQuery(id+"F0.imprint","INTERSECT",VERTEX,{"derivedFrom":[subQ1,subQ0]});Q15=makeQuery(id+"F0.imprint","IMPRINT",FACE,{"disambiguationData":[TD([[makeQuery(id+"F0.imprint","IMPRINT",EDGE,{"disambiguationData":[TD([[subQ2,-1.0]])],"derivedFrom":subQ1}),-1.0]])]});}
            var Q16;
            {var subQ0=sQuery(id+"F0.wireOp",EDGE,"E40.0");var subQ1=sQuery(id+"F0.wireOp",EDGE,"E24");var subQ2=makeQuery(id+"F0.imprint","INTERSECT",VERTEX,{"derivedFrom":[subQ1,subQ0]});Q16=makeQuery(id+"F0.imprint","IMPRINT",FACE,{"disambiguationData":[TD([[makeQuery(id+"F0.imprint","IMPRINT",EDGE,{"disambiguationData":[TD([[subQ2,-1.0]])],"derivedFrom":subQ1}),-1.0]])]});}
            var Q17;
            {var subQ0=sQuery(id+"F0.wireOp",EDGE,"E38.0");var subQ1=sQuery(id+"F0.wireOp",EDGE,"E24");var subQ2=makeQuery(id+"F0.imprint","INTERSECT",VERTEX,{"derivedFrom":[subQ1,subQ0]});Q17=makeQuery(id+"F0.imprint","IMPRINT",FACE,{"disambiguationData":[TD([[makeQuery(id+"F0.imprint","IMPRINT",EDGE,{"disambiguationData":[TD([[subQ2,-1.0]])],"derivedFrom":subQ1}),-1.0]])]});}
            var Q18;
            {var subQ0=sQuery(id+"F0.wireOp",EDGE,"E36.MirrorCS");var subQ1=sQuery(id+"F0.wireOp",EDGE,"E24");var subQ2=makeQuery(id+"F0.imprint","INTERSECT",VERTEX,{"derivedFrom":[subQ1,subQ0]});Q18=makeQuery(id+"F0.imprint","IMPRINT",FACE,{"disambiguationData":[TD([[makeQuery(id+"F0.imprint","IMPRINT",EDGE,{"disambiguationData":[TD([[subQ2,-1.0]])],"derivedFrom":subQ1}),-1.0]])]});}
            var Q19;
            {var subQ0=sQuery(id+"F0.wireOp",EDGE,"E34.MirrorCS");var subQ1=sQuery(id+"F0.wireOp",EDGE,"E24");var subQ2=makeQuery(id+"F0.imprint","INTERSECT",VERTEX,{"derivedFrom":[subQ1,subQ0]});Q19=makeQuery(id+"F0.imprint","IMPRINT",FACE,{"disambiguationData":[TD([[makeQuery(id+"F0.imprint","IMPRINT",EDGE,{"disambiguationData":[TD([[subQ2,-1.0]])],"derivedFrom":subQ1}),-1.0]])]});}
            var Q20;
            {var subQ0=sQuery(id+"F0.wireOp",EDGE,"E32.MirrorCS");var subQ1=sQuery(id+"F0.wireOp",EDGE,"E24");var subQ2=makeQuery(id+"F0.imprint","INTERSECT",VERTEX,{"derivedFrom":[subQ1,subQ0]});Q20=makeQuery(id+"F0.imprint","IMPRINT",FACE,{"disambiguationData":[TD([[makeQuery(id+"F0.imprint","IMPRINT",EDGE,{"disambiguationData":[TD([[subQ2,-1.0]])],"derivedFrom":subQ1}),-1.0]])]});}
            var Q21;
            {var subQ0=sQuery(id+"F0.wireOp",EDGE,"E32.MirrorCS");var subQ1=sQuery(id+"F0.wireOp",EDGE,"E25");var subQ2=makeQuery(id+"F0.imprint","INTERSECT",VERTEX,{"derivedFrom":[subQ1,subQ0]});Q21=makeQuery(id+"F0.imprint","IMPRINT",FACE,{"disambiguationData":[TD([[makeQuery(id+"F0.imprint","IMPRINT",EDGE,{"disambiguationData":[TD([[subQ2,-1.0]])],"derivedFrom":subQ1}),-1.0]])]});}
            var Q22;
            {var subQ0=sQuery(id+"F0.wireOp",EDGE,"E34.MirrorCS");var subQ1=sQuery(id+"F0.wireOp",EDGE,"E25");var subQ2=makeQuery(id+"F0.imprint","INTERSECT",VERTEX,{"derivedFrom":[subQ1,subQ0]});Q22=makeQuery(id+"F0.imprint","IMPRINT",FACE,{"disambiguationData":[TD([[makeQuery(id+"F0.imprint","IMPRINT",EDGE,{"disambiguationData":[TD([[subQ2,-1.0]])],"derivedFrom":subQ1}),-1.0]])]});}
            var Q23;
            {var subQ0=sQuery(id+"F0.wireOp",EDGE,"E36.MirrorCS");var subQ1=sQuery(id+"F0.wireOp",EDGE,"E25");var subQ2=makeQuery(id+"F0.imprint","INTERSECT",VERTEX,{"derivedFrom":[subQ1,subQ0]});Q23=makeQuery(id+"F0.imprint","IMPRINT",FACE,{"disambiguationData":[TD([[makeQuery(id+"F0.imprint","IMPRINT",EDGE,{"disambiguationData":[TD([[subQ2,-1.0]])],"derivedFrom":subQ1}),-1.0]])]});}
            var Q24;
            {var subQ0=sQuery(id+"F0.wireOp",EDGE,"E38.0");var subQ1=sQuery(id+"F0.wireOp",EDGE,"E25");var subQ2=makeQuery(id+"F0.imprint","INTERSECT",VERTEX,{"derivedFrom":[subQ1,subQ0]});Q24=makeQuery(id+"F0.imprint","IMPRINT",FACE,{"disambiguationData":[TD([[makeQuery(id+"F0.imprint","IMPRINT",EDGE,{"disambiguationData":[TD([[subQ2,-1.0]])],"derivedFrom":subQ1}),-1.0]])]});}
            var Q25;
            {var subQ0=sQuery(id+"F0.wireOp",EDGE,"E40.0");var subQ1=sQuery(id+"F0.wireOp",EDGE,"E25");var subQ2=makeQuery(id+"F0.imprint","INTERSECT",VERTEX,{"derivedFrom":[subQ1,subQ0]});Q25=makeQuery(id+"F0.imprint","IMPRINT",FACE,{"disambiguationData":[TD([[makeQuery(id+"F0.imprint","IMPRINT",EDGE,{"disambiguationData":[TD([[subQ2,-1.0]])],"derivedFrom":subQ1}),-1.0]])]});}
            var Q26;
            {var subQ0=sQuery(id+"F0.wireOp",EDGE,"E44.0");var subQ1=sQuery(id+"F0.wireOp",EDGE,"E25");var subQ2=makeQuery(id+"F0.imprint","INTERSECT",VERTEX,{"derivedFrom":[subQ1,subQ0]});Q26=makeQuery(id+"F0.imprint","IMPRINT",FACE,{"disambiguationData":[TD([[makeQuery(id+"F0.imprint","IMPRINT",EDGE,{"disambiguationData":[TD([[subQ2,-1.0]])],"derivedFrom":subQ1}),-1.0]])]});}
            var Q27;
            {var subQ0=sQuery(id+"F0.wireOp",EDGE,"E42.0");var subQ1=sQuery(id+"F0.wireOp",EDGE,"E25");var subQ2=makeQuery(id+"F0.imprint","INTERSECT",VERTEX,{"derivedFrom":[subQ1,subQ0]});Q27=makeQuery(id+"F0.imprint","IMPRINT",FACE,{"disambiguationData":[TD([[makeQuery(id+"F0.imprint","IMPRINT",EDGE,{"disambiguationData":[TD([[subQ2,-1.0]])],"derivedFrom":subQ1}),-1.0]])]});}
            var Q28;
            {var subQ0=sQuery(id+"F0.wireOp",EDGE,"E30.8.0");var subQ1=sQuery(id+"F0.wireOp",EDGE,"E26");var subQ2=makeQuery(id+"F0.imprint","INTERSECT",VERTEX,{"derivedFrom":[subQ1,subQ0]});Q28=makeQuery(id+"F0.imprint","IMPRINT",FACE,{"disambiguationData":[TD([[makeQuery(id+"F0.imprint","IMPRINT",EDGE,{"disambiguationData":[TD([[subQ2,1.0]])],"derivedFrom":subQ1}),-1.0]])]});}
            var Q29;
            {var subQ0=sQuery(id+"F0.wireOp",EDGE,"E42.0");var subQ1=sQuery(id+"F0.wireOp",EDGE,"E26");var subQ2=makeQuery(id+"F0.imprint","INTERSECT",VERTEX,{"derivedFrom":[subQ1,subQ0]});Q29=makeQuery(id+"F0.imprint","IMPRINT",FACE,{"disambiguationData":[TD([[makeQuery(id+"F0.imprint","IMPRINT",EDGE,{"disambiguationData":[TD([[subQ2,-1.0]])],"derivedFrom":subQ1}),-1.0]])]});}
            var Q30;
            {var subQ0=sQuery(id+"F0.wireOp",EDGE,"E43.0");var subQ1=sQuery(id+"F0.wireOp",EDGE,"E26");var subQ2=makeQuery(id+"F0.imprint","INTERSECT",VERTEX,{"derivedFrom":[subQ1,subQ0]});Q30=makeQuery(id+"F0.imprint","IMPRINT",FACE,{"disambiguationData":[TD([[makeQuery(id+"F0.imprint","IMPRINT",EDGE,{"disambiguationData":[TD([[subQ2,-1.0]])],"derivedFrom":subQ1}),-1.0]])]});}
            var Q31;
            {var subQ0=sQuery(id+"F0.wireOp",EDGE,"E44.0");var subQ1=sQuery(id+"F0.wireOp",EDGE,"E26");var subQ2=makeQuery(id+"F0.imprint","INTERSECT",VERTEX,{"derivedFrom":[subQ1,subQ0]});Q31=makeQuery(id+"F0.imprint","IMPRINT",FACE,{"disambiguationData":[TD([[makeQuery(id+"F0.imprint","IMPRINT",EDGE,{"disambiguationData":[TD([[subQ2,-1.0]])],"derivedFrom":subQ1}),-1.0]])]});}
            var Q32;
            {var subQ0=sQuery(id+"F0.wireOp",EDGE,"E39.0");var subQ1=sQuery(id+"F0.wireOp",EDGE,"E26");var subQ2=makeQuery(id+"F0.imprint","INTERSECT",VERTEX,{"derivedFrom":[subQ1,subQ0]});Q32=makeQuery(id+"F0.imprint","IMPRINT",FACE,{"disambiguationData":[TD([[makeQuery(id+"F0.imprint","IMPRINT",EDGE,{"disambiguationData":[TD([[subQ2,-1.0]])],"derivedFrom":subQ1}),-1.0]])]});}
            var Q33;
            {var subQ0=sQuery(id+"F0.wireOp",EDGE,"E40.0");var subQ1=sQuery(id+"F0.wireOp",EDGE,"E26");var subQ2=makeQuery(id+"F0.imprint","INTERSECT",VERTEX,{"derivedFrom":[subQ1,subQ0]});Q33=makeQuery(id+"F0.imprint","IMPRINT",FACE,{"disambiguationData":[TD([[makeQuery(id+"F0.imprint","IMPRINT",EDGE,{"disambiguationData":[TD([[subQ2,-1.0]])],"derivedFrom":subQ1}),-1.0]])]});}
            var Q34;
            {var subQ0=sQuery(id+"F0.wireOp",EDGE,"E37.0");var subQ1=sQuery(id+"F0.wireOp",EDGE,"E26");var subQ2=makeQuery(id+"F0.imprint","INTERSECT",VERTEX,{"derivedFrom":[subQ1,subQ0]});Q34=makeQuery(id+"F0.imprint","IMPRINT",FACE,{"disambiguationData":[TD([[makeQuery(id+"F0.imprint","IMPRINT",EDGE,{"disambiguationData":[TD([[subQ2,-1.0]])],"derivedFrom":subQ1}),-1.0]])]});}
            var Q35;
            {var subQ0=sQuery(id+"F0.wireOp",EDGE,"E38.0");var subQ1=sQuery(id+"F0.wireOp",EDGE,"E26");var subQ2=makeQuery(id+"F0.imprint","INTERSECT",VERTEX,{"derivedFrom":[subQ1,subQ0]});Q35=makeQuery(id+"F0.imprint","IMPRINT",FACE,{"disambiguationData":[TD([[makeQuery(id+"F0.imprint","IMPRINT",EDGE,{"disambiguationData":[TD([[subQ2,-1.0]])],"derivedFrom":subQ1}),-1.0]])]});}
            var Q36;
            {var subQ0=sQuery(id+"F0.wireOp",EDGE,"E35.0");var subQ1=sQuery(id+"F0.wireOp",EDGE,"E26");var subQ2=makeQuery(id+"F0.imprint","INTERSECT",VERTEX,{"derivedFrom":[subQ1,subQ0]});Q36=makeQuery(id+"F0.imprint","IMPRINT",FACE,{"disambiguationData":[TD([[makeQuery(id+"F0.imprint","IMPRINT",EDGE,{"disambiguationData":[TD([[subQ2,-1.0]])],"derivedFrom":subQ1}),-1.0]])]});}
            var Q37;
            {var subQ0=sQuery(id+"F0.wireOp",EDGE,"E36.MirrorCS");var subQ1=sQuery(id+"F0.wireOp",EDGE,"E26");var subQ2=makeQuery(id+"F0.imprint","INTERSECT",VERTEX,{"derivedFrom":[subQ1,subQ0]});Q37=makeQuery(id+"F0.imprint","IMPRINT",FACE,{"disambiguationData":[TD([[makeQuery(id+"F0.imprint","IMPRINT",EDGE,{"disambiguationData":[TD([[subQ2,-1.0]])],"derivedFrom":subQ1}),-1.0]])]});}
            var Q38;
            {var subQ0=sQuery(id+"F0.wireOp",EDGE,"E33.0");var subQ1=sQuery(id+"F0.wireOp",EDGE,"E26");var subQ2=makeQuery(id+"F0.imprint","INTERSECT",VERTEX,{"derivedFrom":[subQ1,subQ0]});Q38=makeQuery(id+"F0.imprint","IMPRINT",FACE,{"disambiguationData":[TD([[makeQuery(id+"F0.imprint","IMPRINT",EDGE,{"disambiguationData":[TD([[subQ2,-1.0]])],"derivedFrom":subQ1}),-1.0]])]});}
            var Q39;
            {var subQ0=sQuery(id+"F0.wireOp",EDGE,"E34.MirrorCS");var subQ1=sQuery(id+"F0.wireOp",EDGE,"E26");var subQ2=makeQuery(id+"F0.imprint","INTERSECT",VERTEX,{"derivedFrom":[subQ1,subQ0]});Q39=makeQuery(id+"F0.imprint","IMPRINT",FACE,{"disambiguationData":[TD([[makeQuery(id+"F0.imprint","IMPRINT",EDGE,{"disambiguationData":[TD([[subQ2,-1.0]])],"derivedFrom":subQ1}),-1.0]])]});}
            var Q40;
            {var subQ0=sQuery(id+"F0.wireOp",EDGE,"E31.0");var subQ1=sQuery(id+"F0.wireOp",EDGE,"E26");var subQ2=makeQuery(id+"F0.imprint","INTERSECT",VERTEX,{"derivedFrom":[subQ1,subQ0]});Q40=makeQuery(id+"F0.imprint","IMPRINT",FACE,{"disambiguationData":[TD([[makeQuery(id+"F0.imprint","IMPRINT",EDGE,{"disambiguationData":[TD([[subQ2,-1.0]])],"derivedFrom":subQ1}),-1.0]])]});}
            var Q41;
            {var subQ0=sQuery(id+"F0.wireOp",EDGE,"E32.MirrorCS");var subQ1=sQuery(id+"F0.wireOp",EDGE,"E26");var subQ2=makeQuery(id+"F0.imprint","INTERSECT",VERTEX,{"derivedFrom":[subQ1,subQ0]});Q41=makeQuery(id+"F0.imprint","IMPRINT",FACE,{"disambiguationData":[TD([[makeQuery(id+"F0.imprint","IMPRINT",EDGE,{"disambiguationData":[TD([[subQ2,-1.0]])],"derivedFrom":subQ1}),-1.0]])]});}
            var Q42;
            {var subQ0=sQuery(id+"F0.wireOp",EDGE,"E29");var subQ1=sQuery(id+"F0.wireOp",EDGE,"E26");var subQ2=makeQuery(id+"F0.imprint","INTERSECT",VERTEX,{"derivedFrom":[subQ1,subQ0]});Q42=makeQuery(id+"F0.imprint","IMPRINT",FACE,{"disambiguationData":[TD([[makeQuery(id+"F0.imprint","IMPRINT",EDGE,{"disambiguationData":[TD([[subQ2,-1.0]])],"derivedFrom":subQ1}),-1.0]])]});}
            var Q43;
            {var subQ13=sQuery(id+"F0.wireOp",EDGE,"E28");Q43=makeQuery(id+"F0.imprint","IMPRINT",FACE,{"disambiguationData":[TD([[makeQuery(id+"F0.imprint","IMPRINT",EDGE,{"derivedFrom":subQ13}),1.0]])]});}
            var Q44;
            {var subQ3=sQuery(id+"F0.wireOp",EDGE,"E34.MirrorCS");var subQ7=sQuery(id+"F0.wireOp",EDGE,"E27");var subQ9=makeQuery(id+"F0.imprint","INTERSECT",VERTEX,{"derivedFrom":[subQ7,subQ3]});Q44=makeQuery(id+"F0.imprint","IMPRINT",FACE,{"disambiguationData":[TD([[makeQuery(id+"F0.imprint","IMPRINT",EDGE,{"disambiguationData":[TD([[subQ9,-1.0]])],"derivedFrom":subQ7}),-1.0]])]});}
            var Q45;
            {var subQ0=sQuery(id+"F0.wireOp",EDGE,"E38.0");var subQ3=sQuery(id+"F0.wireOp",EDGE,"E27");var subQ4=makeQuery(id+"F0.imprint","INTERSECT",VERTEX,{"derivedFrom":[subQ3,subQ0]});Q45=makeQuery(id+"F0.imprint","IMPRINT",FACE,{"disambiguationData":[TD([[makeQuery(id+"F0.imprint","IMPRINT",EDGE,{"disambiguationData":[TD([[subQ4,-1.0]])],"derivedFrom":subQ3}),-1.0]])]});}
            var Q46;
            {var subQ0=sQuery(id+"F0.wireOp",EDGE,"E33.0");var subQ1=sQuery(id+"F0.wireOp",EDGE,"E24");var subQ2=makeQuery(id+"F0.imprint","INTERSECT",VERTEX,{"derivedFrom":[subQ1,subQ0]});Q46=makeQuery(id+"F0.imprint","IMPRINT",FACE,{"disambiguationData":[TD([[makeQuery(id+"F0.imprint","IMPRINT",EDGE,{"disambiguationData":[TD([[subQ2,-1.0]])],"derivedFrom":subQ1}),-1.0]])]});}
            extrude(context, id + "F2", {"entities" : qUnion([Q0, Q1, Q2, Q3, Q4, Q5, Q6, Q7, Q8, Q9, Q10, Q11, Q12, Q13, Q14, Q15, Q16, Q17, Q18, Q19, Q20, Q21, Q22, Q23, Q24, Q25, Q26, Q27, Q28, Q29, Q30, Q31, Q32, Q33, Q34, Q35, Q36, Q37, Q38, Q39, Q40, Q41, Q42, Q43, Q44, Q45, Q46]), "operationType" : NewBodyOperationType.ADD, "depth" : 1.5 * mm});
        }
        {
            var Q0;
            {var subQ31=sQuery(id+"F0.wireOp",EDGE,"E13.right");Q0=makeQuery(id+"F0.imprint","IMPRINT",FACE,{"disambiguationData":[TD([[makeQuery(id+"F0.imprint","IMPRINT",EDGE,{"derivedFrom":subQ31}),1.0]])]});}
            extrude(context, id + "F3", {"entities" : qUnion([Q0]), "operationType" : NewBodyOperationType.ADD, "depth" : 2 * mm});
        }
        {
            var Q0;
            Q0=makeQuery(id+"F3.opExtrude","CAP_EDGE",EDGE,{"disambiguationData":[OSD([sQuery(id+"F0.wireOp",EDGE,"E18.4.5.4")])],"isStart":false});
            var Q1;
            Q1=makeQuery(id+"F3.opExtrude","CAP_EDGE",EDGE,{"disambiguationData":[OSD([sQuery(id+"F0.wireOp",EDGE,"E18.4.5.3")])],"isStart":false});
            var Q2;
            Q2=makeQuery(id+"F3.opExtrude","CAP_EDGE",EDGE,{"disambiguationData":[OSD([sQuery(id+"F0.wireOp",EDGE,"E18.3.5.4")])],"isStart":false});
            var Q3;
            Q3=makeQuery(id+"F3.opExtrude","CAP_EDGE",EDGE,{"disambiguationData":[OSD([sQuery(id+"F0.wireOp",EDGE,"E18.3.5.3")])],"isStart":false});
            var Q4;
            Q4=makeQuery(id+"F3.opExtrude","CAP_EDGE",EDGE,{"disambiguationData":[OSD([sQuery(id+"F0.wireOp",EDGE,"E18.2.5.4")])],"isStart":false});
            var Q5;
            Q5=makeQuery(id+"F3.opExtrude","CAP_EDGE",EDGE,{"disambiguationData":[OSD([sQuery(id+"F0.wireOp",EDGE,"E18.2.5.3")])],"isStart":false});
            var Q6;
            Q6=makeQuery(id+"F3.opExtrude","CAP_EDGE",EDGE,{"disambiguationData":[OSD([sQuery(id+"F0.wireOp",EDGE,"E18.1.5.4")])],"isStart":false});
            var Q7;
            Q7=makeQuery(id+"F3.opExtrude","CAP_EDGE",EDGE,{"disambiguationData":[OSD([sQuery(id+"F0.wireOp",EDGE,"E18.1.5.3")])],"isStart":false});
            var Q8;
            Q8=makeQuery(id+"F3.opExtrude","CAP_EDGE",EDGE,{"disambiguationData":[OSD([sQuery(id+"F0.wireOp",EDGE,"E18.1.4.1")])],"isStart":false});
            var Q9;
            Q9=makeQuery(id+"F3.opExtrude","CAP_EDGE",EDGE,{"disambiguationData":[OSD([sQuery(id+"F0.wireOp",EDGE,"E18.1.4.2")])],"isStart":false});
            var Q10;
            Q10=makeQuery(id+"F3.opExtrude","CAP_EDGE",EDGE,{"disambiguationData":[OSD([sQuery(id+"F0.wireOp",EDGE,"E18.1.4.3")])],"isStart":false});
            var Q11;
            Q11=makeQuery(id+"F3.opExtrude","CAP_EDGE",EDGE,{"disambiguationData":[OSD([sQuery(id+"F0.wireOp",EDGE,"E18.1.4.4")])],"isStart":false});
            var Q12;
            Q12=makeQuery(id+"F3.opExtrude","CAP_EDGE",EDGE,{"disambiguationData":[OSD([sQuery(id+"F0.wireOp",EDGE,"E18.2.4.2")])],"isStart":false});
            var Q13;
            Q13=makeQuery(id+"F3.opExtrude","CAP_EDGE",EDGE,{"disambiguationData":[OSD([sQuery(id+"F0.wireOp",EDGE,"E18.2.4.1")])],"isStart":false});
            var Q14;
            Q14=makeQuery(id+"F3.opExtrude","CAP_EDGE",EDGE,{"disambiguationData":[OSD([sQuery(id+"F0.wireOp",EDGE,"E18.3.4.2")])],"isStart":false});
            var Q15;
            Q15=makeQuery(id+"F3.opExtrude","CAP_EDGE",EDGE,{"disambiguationData":[OSD([sQuery(id+"F0.wireOp",EDGE,"E18.3.4.1")])],"isStart":false});
            var Q16;
            Q16=makeQuery(id+"F3.opExtrude","CAP_EDGE",EDGE,{"disambiguationData":[OSD([sQuery(id+"F0.wireOp",EDGE,"E18.4.4.1")])],"isStart":false});
            var Q17;
            Q17=makeQuery(id+"F3.opExtrude","CAP_EDGE",EDGE,{"disambiguationData":[OSD([sQuery(id+"F0.wireOp",EDGE,"E18.4.4.2")])],"isStart":false});
            var Q18;
            Q18=makeQuery(id+"F3.opExtrude","CAP_EDGE",EDGE,{"disambiguationData":[OSD([sQuery(id+"F0.wireOp",EDGE,"E18.5.4.1")])],"isStart":false});
            var Q19;
            Q19=makeQuery(id+"F3.opExtrude","CAP_EDGE",EDGE,{"disambiguationData":[OSD([sQuery(id+"F0.wireOp",EDGE,"E18.5.4.2")])],"isStart":false});
            var Q20;
            Q20=makeQuery(id+"F3.opExtrude","CAP_EDGE",EDGE,{"disambiguationData":[OSD([sQuery(id+"F0.wireOp",EDGE,"E18.4.4.4")])],"isStart":false});
            var Q21;
            Q21=makeQuery(id+"F3.opExtrude","CAP_EDGE",EDGE,{"disambiguationData":[OSD([sQuery(id+"F0.wireOp",EDGE,"E18.4.4.3")])],"isStart":false});
            var Q22;
            Q22=makeQuery(id+"F3.opExtrude","CAP_EDGE",EDGE,{"disambiguationData":[OSD([sQuery(id+"F0.wireOp",EDGE,"E18.4.3.4")])],"isStart":false});
            var Q23;
            Q23=makeQuery(id+"F3.opExtrude","CAP_EDGE",EDGE,{"disambiguationData":[OSD([sQuery(id+"F0.wireOp",EDGE,"E18.4.3.3")])],"isStart":false});
            var Q24;
            Q24=makeQuery(id+"F3.opExtrude","CAP_EDGE",EDGE,{"disambiguationData":[OSD([sQuery(id+"F0.wireOp",EDGE,"E18.3.3.4")])],"isStart":false});
            var Q25;
            Q25=makeQuery(id+"F3.opExtrude","CAP_EDGE",EDGE,{"disambiguationData":[OSD([sQuery(id+"F0.wireOp",EDGE,"E18.3.4.4")])],"isStart":false});
            var Q26;
            Q26=makeQuery(id+"F3.opExtrude","CAP_EDGE",EDGE,{"disambiguationData":[OSD([sQuery(id+"F0.wireOp",EDGE,"E18.3.4.3")])],"isStart":false});
            var Q27;
            Q27=makeQuery(id+"F3.opExtrude","CAP_EDGE",EDGE,{"disambiguationData":[OSD([sQuery(id+"F0.wireOp",EDGE,"E18.2.4.4")])],"isStart":false});
            var Q28;
            Q28=makeQuery(id+"F3.opExtrude","CAP_EDGE",EDGE,{"disambiguationData":[OSD([sQuery(id+"F0.wireOp",EDGE,"E18.2.4.3")])],"isStart":false});
            var Q29;
            Q29=makeQuery(id+"F3.opExtrude","CAP_EDGE",EDGE,{"disambiguationData":[OSD([sQuery(id+"F0.wireOp",EDGE,"E18.2.3.4")])],"isStart":false});
            var Q30;
            Q30=makeQuery(id+"F3.opExtrude","CAP_EDGE",EDGE,{"disambiguationData":[OSD([sQuery(id+"F0.wireOp",EDGE,"E18.2.3.3")])],"isStart":false});
            var Q31;
            Q31=makeQuery(id+"F3.opExtrude","CAP_EDGE",EDGE,{"disambiguationData":[OSD([sQuery(id+"F0.wireOp",EDGE,"E18.1.3.4")])],"isStart":false});
            var Q32;
            Q32=makeQuery(id+"F3.opExtrude","CAP_EDGE",EDGE,{"disambiguationData":[OSD([sQuery(id+"F0.wireOp",EDGE,"E18.1.3.3")])],"isStart":false});
            var Q33;
            Q33=makeQuery(id+"F3.opExtrude","CAP_EDGE",EDGE,{"disambiguationData":[OSD([sQuery(id+"F0.wireOp",EDGE,"E18.0.3.4")])],"isStart":false});
            var Q34;
            Q34=makeQuery(id+"F3.opExtrude","CAP_EDGE",EDGE,{"disambiguationData":[OSD([sQuery(id+"F0.wireOp",EDGE,"E18.0.3.3")])],"isStart":false});
            var Q35;
            Q35=makeQuery(id+"F3.opExtrude","CAP_EDGE",EDGE,{"disambiguationData":[OSD([sQuery(id+"F0.wireOp",EDGE,"E18.0.4.4")])],"isStart":false});
            var Q36;
            Q36=makeQuery(id+"F3.opExtrude","CAP_EDGE",EDGE,{"disambiguationData":[OSD([sQuery(id+"F0.wireOp",EDGE,"E18.0.4.3")])],"isStart":false});
            var Q37;
            Q37=makeQuery(id+"F3.opExtrude","CAP_EDGE",EDGE,{"disambiguationData":[OSD([sQuery(id+"F0.wireOp",EDGE,"E18.0.5.4")])],"isStart":false});
            var Q38;
            Q38=makeQuery(id+"F3.opExtrude","CAP_EDGE",EDGE,{"disambiguationData":[OSD([sQuery(id+"F0.wireOp",EDGE,"E18.0.5.3")])],"isStart":false});
            var Q39;
            Q39=makeQuery(id+"F3.opExtrude","CAP_EDGE",EDGE,{"disambiguationData":[OSD([sQuery(id+"F0.wireOp",EDGE,"E18.0.4.1")])],"isStart":false});
            var Q40;
            Q40=makeQuery(id+"F3.opExtrude","CAP_EDGE",EDGE,{"disambiguationData":[OSD([sQuery(id+"F0.wireOp",EDGE,"E18.0.4.2")])],"isStart":false});
            var Q41;
            Q41=makeQuery(id+"F3.opExtrude","CAP_EDGE",EDGE,{"disambiguationData":[OSD([sQuery(id+"F0.wireOp",EDGE,"E18.0.3.2")])],"isStart":false});
            var Q42;
            Q42=makeQuery(id+"F3.opExtrude","CAP_EDGE",EDGE,{"disambiguationData":[OSD([sQuery(id+"F0.wireOp",EDGE,"E18.0.3.1")])],"isStart":false});
            var Q43;
            Q43=makeQuery(id+"F3.opExtrude","CAP_EDGE",EDGE,{"disambiguationData":[OSD([sQuery(id+"F0.wireOp",EDGE,"E18.1.3.2")])],"isStart":false});
            var Q44;
            Q44=makeQuery(id+"F3.opExtrude","CAP_EDGE",EDGE,{"disambiguationData":[OSD([sQuery(id+"F0.wireOp",EDGE,"E18.1.3.1")])],"isStart":false});
            var Q45;
            Q45=makeQuery(id+"F3.opExtrude","CAP_EDGE",EDGE,{"disambiguationData":[OSD([sQuery(id+"F0.wireOp",EDGE,"E18.2.3.2")])],"isStart":false});
            var Q46;
            Q46=makeQuery(id+"F3.opExtrude","CAP_EDGE",EDGE,{"disambiguationData":[OSD([sQuery(id+"F0.wireOp",EDGE,"E18.2.3.1")])],"isStart":false});
            var Q47;
            Q47=makeQuery(id+"F3.opExtrude","CAP_EDGE",EDGE,{"disambiguationData":[OSD([sQuery(id+"F0.wireOp",EDGE,"E18.3.3.2")])],"isStart":false});
            var Q48;
            Q48=makeQuery(id+"F3.opExtrude","CAP_EDGE",EDGE,{"disambiguationData":[OSD([sQuery(id+"F0.wireOp",EDGE,"E18.3.3.1")])],"isStart":false});
            var Q49;
            Q49=makeQuery(id+"F3.opExtrude","CAP_EDGE",EDGE,{"disambiguationData":[OSD([sQuery(id+"F0.wireOp",EDGE,"E18.4.3.2")])],"isStart":false});
            var Q50;
            Q50=makeQuery(id+"F3.opExtrude","CAP_EDGE",EDGE,{"disambiguationData":[OSD([sQuery(id+"F0.wireOp",EDGE,"E18.4.3.1")])],"isStart":false});
            var Q51;
            Q51=makeQuery(id+"F3.opExtrude","CAP_EDGE",EDGE,{"disambiguationData":[OSD([sQuery(id+"F0.wireOp",EDGE,"E18.3.3.3")])],"isStart":false});
            var Q52;
            Q52=makeQuery(id+"F3.opExtrude","CAP_EDGE",EDGE,{"disambiguationData":[OSD([sQuery(id+"F0.wireOp",EDGE,"E18.5.3.1")])],"isStart":false});
            var Q53;
            Q53=makeQuery(id+"F3.opExtrude","CAP_EDGE",EDGE,{"disambiguationData":[OSD([sQuery(id+"F0.wireOp",EDGE,"E18.5.3.2")])],"isStart":false});
            var Q54;
            Q54=makeQuery(id+"F3.opExtrude","CAP_EDGE",EDGE,{"disambiguationData":[OSD([sQuery(id+"F0.wireOp",EDGE,"E18.5.2.1")])],"isStart":false});
            var Q55;
            Q55=makeQuery(id+"F3.opExtrude","CAP_EDGE",EDGE,{"disambiguationData":[OSD([sQuery(id+"F0.wireOp",EDGE,"E18.5.2.2")])],"isStart":false});
            var Q56;
            Q56=makeQuery(id+"F3.opExtrude","CAP_EDGE",EDGE,{"disambiguationData":[OSD([sQuery(id+"F0.wireOp",EDGE,"E18.4.2.4")])],"isStart":false});
            var Q57;
            Q57=makeQuery(id+"F3.opExtrude","CAP_EDGE",EDGE,{"disambiguationData":[OSD([sQuery(id+"F0.wireOp",EDGE,"E18.4.2.3")])],"isStart":false});
            var Q58;
            Q58=makeQuery(id+"F3.opExtrude","CAP_EDGE",EDGE,{"disambiguationData":[OSD([sQuery(id+"F0.wireOp",EDGE,"E18.4.2.1")])],"isStart":false});
            var Q59;
            Q59=makeQuery(id+"F3.opExtrude","CAP_EDGE",EDGE,{"disambiguationData":[OSD([sQuery(id+"F0.wireOp",EDGE,"E18.4.2.2")])],"isStart":false});
            var Q60;
            Q60=makeQuery(id+"F3.opExtrude","CAP_EDGE",EDGE,{"disambiguationData":[OSD([sQuery(id+"F0.wireOp",EDGE,"E18.3.2.1")])],"isStart":false});
            var Q61;
            Q61=makeQuery(id+"F3.opExtrude","CAP_EDGE",EDGE,{"disambiguationData":[OSD([sQuery(id+"F0.wireOp",EDGE,"E18.3.2.2")])],"isStart":false});
            var Q62;
            Q62=makeQuery(id+"F3.opExtrude","CAP_EDGE",EDGE,{"disambiguationData":[OSD([sQuery(id+"F0.wireOp",EDGE,"E18.2.2.1")])],"isStart":false});
            var Q63;
            Q63=makeQuery(id+"F3.opExtrude","CAP_EDGE",EDGE,{"disambiguationData":[OSD([sQuery(id+"F0.wireOp",EDGE,"E18.2.2.2")])],"isStart":false});
            var Q64;
            Q64=makeQuery(id+"F3.opExtrude","CAP_EDGE",EDGE,{"disambiguationData":[OSD([sQuery(id+"F0.wireOp",EDGE,"E18.1.2.1")])],"isStart":false});
            var Q65;
            Q65=makeQuery(id+"F3.opExtrude","CAP_EDGE",EDGE,{"disambiguationData":[OSD([sQuery(id+"F0.wireOp",EDGE,"E18.1.2.2")])],"isStart":false});
            var Q66;
            Q66=makeQuery(id+"F3.opExtrude","CAP_EDGE",EDGE,{"disambiguationData":[OSD([sQuery(id+"F0.wireOp",EDGE,"E18.0.2.1")])],"isStart":false});
            var Q67;
            Q67=makeQuery(id+"F3.opExtrude","CAP_EDGE",EDGE,{"disambiguationData":[OSD([sQuery(id+"F0.wireOp",EDGE,"E18.0.2.2")])],"isStart":false});
            var Q68;
            Q68=makeQuery(id+"F3.opExtrude","CAP_EDGE",EDGE,{"disambiguationData":[OSD([sQuery(id+"F0.wireOp",EDGE,"E18.0.2.3")])],"isStart":false});
            var Q69;
            Q69=makeQuery(id+"F3.opExtrude","CAP_EDGE",EDGE,{"disambiguationData":[OSD([sQuery(id+"F0.wireOp",EDGE,"E18.0.2.4")])],"isStart":false});
            var Q70;
            Q70=makeQuery(id+"F3.opExtrude","CAP_EDGE",EDGE,{"disambiguationData":[OSD([sQuery(id+"F0.wireOp",EDGE,"E18.0.1.1")])],"isStart":false});
            var Q71;
            Q71=makeQuery(id+"F3.opExtrude","CAP_EDGE",EDGE,{"disambiguationData":[OSD([sQuery(id+"F0.wireOp",EDGE,"E18.0.1.2")])],"isStart":false});
            var Q72;
            Q72=makeQuery(id+"F3.opExtrude","CAP_EDGE",EDGE,{"disambiguationData":[OSD([sQuery(id+"F0.wireOp",EDGE,"E15.top")])],"isStart":false});
            var Q73;
            Q73=makeQuery(id+"F3.opExtrude","CAP_EDGE",EDGE,{"disambiguationData":[OSD([sQuery(id+"F0.wireOp",EDGE,"E13.top")])],"isStart":false});
            var Q74;
            Q74=makeQuery(id+"F3.opExtrude","CAP_EDGE",EDGE,{"disambiguationData":[OSD([sQuery(id+"F0.wireOp",EDGE,"E18.0.1.3")])],"isStart":false});
            var Q75;
            Q75=makeQuery(id+"F3.opExtrude","CAP_EDGE",EDGE,{"disambiguationData":[OSD([sQuery(id+"F0.wireOp",EDGE,"E18.0.1.4")])],"isStart":false});
            var Q76;
            Q76=makeQuery(id+"F3.opExtrude","CAP_EDGE",EDGE,{"disambiguationData":[OSD([sQuery(id+"F0.wireOp",EDGE,"E13.right")])],"isStart":false});
            var Q77;
            Q77=makeQuery(id+"F3.opExtrude","CAP_EDGE",EDGE,{"disambiguationData":[OSD([sQuery(id+"F0.wireOp",EDGE,"E14.right")])],"isStart":false});
            var Q78;
            Q78=makeQuery(id+"F3.opExtrude","CAP_EDGE",EDGE,{"disambiguationData":[OSD([sQuery(id+"F0.wireOp",EDGE,"E18.1.0.2")])],"isStart":false});
            var Q79;
            Q79=makeQuery(id+"F3.opExtrude","CAP_EDGE",EDGE,{"disambiguationData":[OSD([sQuery(id+"F0.wireOp",EDGE,"E18.1.0.1")])],"isStart":false});
            var Q80;
            Q80=makeQuery(id+"F3.opExtrude","CAP_EDGE",EDGE,{"disambiguationData":[OSD([sQuery(id+"F0.wireOp",EDGE,"E18.1.1.2")])],"isStart":false});
            var Q81;
            Q81=makeQuery(id+"F3.opExtrude","CAP_EDGE",EDGE,{"disambiguationData":[OSD([sQuery(id+"F0.wireOp",EDGE,"E18.1.1.1")])],"isStart":false});
            var Q82;
            Q82=makeQuery(id+"F3.opExtrude","CAP_EDGE",EDGE,{"disambiguationData":[OSD([sQuery(id+"F0.wireOp",EDGE,"E18.1.0.3")])],"isStart":false});
            var Q83;
            Q83=makeQuery(id+"F3.opExtrude","CAP_EDGE",EDGE,{"disambiguationData":[OSD([sQuery(id+"F0.wireOp",EDGE,"E18.1.0.4")])],"isStart":false});
            var Q84;
            Q84=makeQuery(id+"F3.opExtrude","CAP_EDGE",EDGE,{"disambiguationData":[OSD([sQuery(id+"F0.wireOp",EDGE,"E18.1.1.4")])],"isStart":false});
            var Q85;
            Q85=makeQuery(id+"F3.opExtrude","CAP_EDGE",EDGE,{"disambiguationData":[OSD([sQuery(id+"F0.wireOp",EDGE,"E18.1.1.3")])],"isStart":false});
            var Q86;
            Q86=makeQuery(id+"F3.opExtrude","CAP_EDGE",EDGE,{"disambiguationData":[OSD([sQuery(id+"F0.wireOp",EDGE,"E18.1.2.4")])],"isStart":false});
            var Q87;
            Q87=makeQuery(id+"F3.opExtrude","CAP_EDGE",EDGE,{"disambiguationData":[OSD([sQuery(id+"F0.wireOp",EDGE,"E18.1.2.3")])],"isStart":false});
            var Q88;
            Q88=makeQuery(id+"F3.opExtrude","CAP_EDGE",EDGE,{"disambiguationData":[OSD([sQuery(id+"F0.wireOp",EDGE,"E18.2.1.1")])],"isStart":false});
            var Q89;
            Q89=makeQuery(id+"F3.opExtrude","CAP_EDGE",EDGE,{"disambiguationData":[OSD([sQuery(id+"F0.wireOp",EDGE,"E18.2.1.2")])],"isStart":false});
            var Q90;
            Q90=makeQuery(id+"F3.opExtrude","CAP_EDGE",EDGE,{"disambiguationData":[OSD([sQuery(id+"F0.wireOp",EDGE,"E18.2.0.1")])],"isStart":false});
            var Q91;
            Q91=makeQuery(id+"F3.opExtrude","CAP_EDGE",EDGE,{"disambiguationData":[OSD([sQuery(id+"F0.wireOp",EDGE,"E18.2.0.2")])],"isStart":false});
            var Q92;
            Q92=makeQuery(id+"F3.opExtrude","CAP_EDGE",EDGE,{"disambiguationData":[OSD([sQuery(id+"F0.wireOp",EDGE,"E18.2.2.3")])],"isStart":false});
            var Q93;
            Q93=makeQuery(id+"F3.opExtrude","CAP_EDGE",EDGE,{"disambiguationData":[OSD([sQuery(id+"F0.wireOp",EDGE,"E18.2.2.4")])],"isStart":false});
            var Q94;
            Q94=makeQuery(id+"F3.opExtrude","CAP_EDGE",EDGE,{"disambiguationData":[OSD([sQuery(id+"F0.wireOp",EDGE,"E18.2.1.4")])],"isStart":false});
            var Q95;
            Q95=makeQuery(id+"F3.opExtrude","CAP_EDGE",EDGE,{"disambiguationData":[OSD([sQuery(id+"F0.wireOp",EDGE,"E18.2.1.3")])],"isStart":false});
            var Q96;
            Q96=makeQuery(id+"F3.opExtrude","CAP_EDGE",EDGE,{"disambiguationData":[OSD([sQuery(id+"F0.wireOp",EDGE,"E18.2.0.4")])],"isStart":false});
            var Q97;
            Q97=makeQuery(id+"F3.opExtrude","CAP_EDGE",EDGE,{"disambiguationData":[OSD([sQuery(id+"F0.wireOp",EDGE,"E18.2.0.3")])],"isStart":false});
            var Q98;
            Q98=makeQuery(id+"F3.opExtrude","CAP_EDGE",EDGE,{"disambiguationData":[OSD([sQuery(id+"F0.wireOp",EDGE,"E18.3.0.2")])],"isStart":false});
            var Q99;
            Q99=makeQuery(id+"F3.opExtrude","CAP_EDGE",EDGE,{"disambiguationData":[OSD([sQuery(id+"F0.wireOp",EDGE,"E18.3.0.1")])],"isStart":false});
            var Q100;
            Q100=makeQuery(id+"F3.opExtrude","CAP_EDGE",EDGE,{"disambiguationData":[OSD([sQuery(id+"F0.wireOp",EDGE,"E18.3.1.2")])],"isStart":false});
            var Q101;
            Q101=makeQuery(id+"F3.opExtrude","CAP_EDGE",EDGE,{"disambiguationData":[OSD([sQuery(id+"F0.wireOp",EDGE,"E18.3.1.1")])],"isStart":false});
            var Q102;
            Q102=makeQuery(id+"F3.opExtrude","CAP_EDGE",EDGE,{"disambiguationData":[OSD([sQuery(id+"F0.wireOp",EDGE,"E18.3.0.3")])],"isStart":false});
            var Q103;
            Q103=makeQuery(id+"F3.opExtrude","CAP_EDGE",EDGE,{"disambiguationData":[OSD([sQuery(id+"F0.wireOp",EDGE,"E18.3.0.4")])],"isStart":false});
            var Q104;
            Q104=makeQuery(id+"F3.opExtrude","CAP_EDGE",EDGE,{"disambiguationData":[OSD([sQuery(id+"F0.wireOp",EDGE,"E18.3.1.4")])],"isStart":false});
            var Q105;
            Q105=makeQuery(id+"F3.opExtrude","CAP_EDGE",EDGE,{"disambiguationData":[OSD([sQuery(id+"F0.wireOp",EDGE,"E18.3.1.3")])],"isStart":false});
            var Q106;
            Q106=makeQuery(id+"F3.opExtrude","CAP_EDGE",EDGE,{"disambiguationData":[OSD([sQuery(id+"F0.wireOp",EDGE,"E18.3.2.3")])],"isStart":false});
            var Q107;
            Q107=makeQuery(id+"F3.opExtrude","CAP_EDGE",EDGE,{"disambiguationData":[OSD([sQuery(id+"F0.wireOp",EDGE,"E18.3.2.4")])],"isStart":false});
            var Q108;
            Q108=makeQuery(id+"F3.opExtrude","CAP_EDGE",EDGE,{"disambiguationData":[OSD([sQuery(id+"F0.wireOp",EDGE,"E18.4.1.2")])],"isStart":false});
            var Q109;
            Q109=makeQuery(id+"F3.opExtrude","CAP_EDGE",EDGE,{"disambiguationData":[OSD([sQuery(id+"F0.wireOp",EDGE,"E18.4.1.1")])],"isStart":false});
            var Q110;
            Q110=makeQuery(id+"F3.opExtrude","CAP_EDGE",EDGE,{"disambiguationData":[OSD([sQuery(id+"F0.wireOp",EDGE,"E18.4.1.4")])],"isStart":false});
            var Q111;
            Q111=makeQuery(id+"F3.opExtrude","CAP_EDGE",EDGE,{"disambiguationData":[OSD([sQuery(id+"F0.wireOp",EDGE,"E18.4.1.3")])],"isStart":false});
            var Q112;
            Q112=makeQuery(id+"F3.opExtrude","CAP_EDGE",EDGE,{"disambiguationData":[OSD([sQuery(id+"F0.wireOp",EDGE,"E18.5.1.2")])],"isStart":false});
            var Q113;
            Q113=makeQuery(id+"F3.opExtrude","CAP_EDGE",EDGE,{"disambiguationData":[OSD([sQuery(id+"F0.wireOp",EDGE,"E18.5.1.1")])],"isStart":false});
            var Q114;
            Q114=makeQuery(id+"F3.opExtrude","CAP_EDGE",EDGE,{"disambiguationData":[OSD([sQuery(id+"F0.wireOp",EDGE,"E18.5.0.1")])],"isStart":false});
            var Q115;
            Q115=makeQuery(id+"F3.opExtrude","CAP_EDGE",EDGE,{"disambiguationData":[OSD([sQuery(id+"F0.wireOp",EDGE,"E18.5.0.2")])],"isStart":false});
            var Q116;
            Q116=makeQuery(id+"F3.opExtrude","CAP_EDGE",EDGE,{"disambiguationData":[OSD([sQuery(id+"F0.wireOp",EDGE,"E18.4.0.4")])],"isStart":false});
            var Q117;
            Q117=makeQuery(id+"F3.opExtrude","CAP_EDGE",EDGE,{"disambiguationData":[OSD([sQuery(id+"F0.wireOp",EDGE,"E18.4.0.3")])],"isStart":false});
            var Q118;
            Q118=makeQuery(id+"F3.opExtrude","CAP_EDGE",EDGE,{"disambiguationData":[OSD([sQuery(id+"F0.wireOp",EDGE,"E18.4.0.1")])],"isStart":false});
            var Q119;
            Q119=makeQuery(id+"F3.opExtrude","CAP_EDGE",EDGE,{"disambiguationData":[OSD([sQuery(id+"F0.wireOp",EDGE,"E18.4.0.2")])],"isStart":false});
            fillet(context, id + "F4", {"entities" : qUnion([Q0, Q1, Q2, Q3, Q4, Q5, Q6, Q7, Q8, Q9, Q10, Q11, Q12, Q13, Q14, Q15, Q16, Q17, Q18, Q19, Q20, Q21, Q22, Q23, Q24, Q25, Q26, Q27, Q28, Q29, Q30, Q31, Q32, Q33, Q34, Q35, Q36, Q37, Q38, Q39, Q40, Q41, Q42, Q43, Q44, Q45, Q46, Q47, Q48, Q49, Q50, Q51, Q52, Q53, Q54, Q55, Q56, Q57, Q58, Q59, Q60, Q61, Q62, Q63, Q64, Q65, Q66, Q67, Q68, Q69, Q70, Q71, Q72, Q73, Q74, Q75, Q76, Q77, Q78, Q79, Q80, Q81, Q82, Q83, Q84, Q85, Q86, Q87, Q88, Q89, Q90, Q91, Q92, Q93, Q94, Q95, Q96, Q97, Q98, Q99, Q100, Q101, Q102, Q103, Q104, Q105, Q106, Q107, Q108, Q109, Q110, Q111, Q112, Q113, Q114, Q115, Q116, Q117, Q118, Q119]), "radius" : 0.5 * mm, "tangentPropagation" : true, "allowEdgeOverflow" : false});
        }
        {
            var Q0;
            {var subQ0=sQuery(id+"F0.wireOp",EDGE,"E25");Q0=makeQuery(id+"F2.opExtrude","CAP_EDGE",EDGE,{"disambiguationData":[OSD([subQ0]),TDD([makeQuery(id+"F0.imprint","IMPRINT",EDGE,{"disambiguationData":[TD([[makeQuery(id+"F0.imprint","INTERSECT",VERTEX,{"derivedFrom":[subQ0,sQuery(id+"F0.wireOp",EDGE,"E29")]}),-1.0]])],"derivedFrom":subQ0})])],"isStart":false});}
            var Q1;
            {var subQ0=sQuery(id+"F0.wireOp",EDGE,"E24");Q1=makeQuery(id+"F2.opExtrude","CAP_EDGE",EDGE,{"disambiguationData":[OSD([subQ0]),TDD([makeQuery(id+"F0.imprint","IMPRINT",EDGE,{"disambiguationData":[TD([[makeQuery(id+"F0.imprint","INTERSECT",VERTEX,{"derivedFrom":[subQ0,sQuery(id+"F0.wireOp",EDGE,"E29")]}),-1.0]])],"derivedFrom":subQ0})])],"isStart":false});}
            var Q2;
            {var subQ0=sQuery(id+"F0.wireOp",EDGE,"E32.MirrorCS");Q2=makeQuery(id+"F2.opExtrude","CAP_EDGE",EDGE,{"disambiguationData":[OSD([subQ0]),TDD([makeQuery(id+"F0.imprint","IMPRINT",EDGE,{"disambiguationData":[TD([[makeQuery(id+"F0.imprint","INTERSECT",VERTEX,{"derivedFrom":[sQuery(id+"F0.wireOp",EDGE,"E22"),subQ0]}),1.0]])],"derivedFrom":subQ0})])],"isStart":false});}
            var Q3;
            {var subQ0=sQuery(id+"F0.wireOp",EDGE,"E31.0");Q3=makeQuery(id+"F2.opExtrude","CAP_EDGE",EDGE,{"disambiguationData":[OSD([subQ0]),TDD([makeQuery(id+"F0.imprint","IMPRINT",EDGE,{"disambiguationData":[TD([[makeQuery(id+"F0.imprint","INTERSECT",VERTEX,{"derivedFrom":[sQuery(id+"F0.wireOp",EDGE,"E25"),subQ0]}),1.0]])],"derivedFrom":subQ0})])],"isStart":false});}
            var Q4;
            {var subQ0=sQuery(id+"F0.wireOp",EDGE,"E32.MirrorCS");Q4=makeQuery(id+"F2.opExtrude","CAP_EDGE",EDGE,{"disambiguationData":[OSD([subQ0]),TDD([makeQuery(id+"F0.imprint","IMPRINT",EDGE,{"disambiguationData":[TD([[makeQuery(id+"F0.imprint","INTERSECT",VERTEX,{"derivedFrom":[sQuery(id+"F0.wireOp",EDGE,"E25"),subQ0]}),1.0]])],"derivedFrom":subQ0})])],"isStart":false});}
            var Q5;
            {var subQ0=sQuery(id+"F0.wireOp",EDGE,"E26");Q5=makeQuery(id+"F2.opExtrude","CAP_EDGE",EDGE,{"disambiguationData":[OSD([subQ0]),TDD([makeQuery(id+"F0.imprint","IMPRINT",EDGE,{"disambiguationData":[TD([[makeQuery(id+"F0.imprint","INTERSECT",VERTEX,{"derivedFrom":[subQ0,sQuery(id+"F0.wireOp",EDGE,"E29")]}),-1.0]])],"derivedFrom":subQ0})])],"isStart":false});}
            var Q6;
            {var subQ0=sQuery(id+"F0.wireOp",EDGE,"E27");Q6=makeQuery(id+"F2.opExtrude","CAP_EDGE",EDGE,{"disambiguationData":[OSD([subQ0]),TDD([makeQuery(id+"F0.imprint","IMPRINT",EDGE,{"disambiguationData":[TD([[makeQuery(id+"F0.imprint","INTERSECT",VERTEX,{"derivedFrom":[subQ0,sQuery(id+"F0.wireOp",EDGE,"E31.0")]}),-1.0]])],"derivedFrom":subQ0})])],"isStart":false});}
            var Q7;
            {var subQ0=sQuery(id+"F0.wireOp",EDGE,"E32.MirrorCS");Q7=makeQuery(id+"F2.opExtrude","CAP_EDGE",EDGE,{"disambiguationData":[OSD([subQ0]),TDD([makeQuery(id+"F0.imprint","IMPRINT",EDGE,{"disambiguationData":[TD([[makeQuery(id+"F0.imprint","INTERSECT",VERTEX,{"derivedFrom":[sQuery(id+"F0.wireOp",EDGE,"E29"),subQ0]}),-1.0]])],"derivedFrom":subQ0})])],"isStart":false});}
            var Q8;
            {var subQ0=sQuery(id+"F0.wireOp",EDGE,"E31.0");Q8=makeQuery(id+"F2.opExtrude","CAP_EDGE",EDGE,{"disambiguationData":[OSD([subQ0]),TDD([makeQuery(id+"F0.imprint","IMPRINT",EDGE,{"disambiguationData":[TD([[makeQuery(id+"F0.imprint","INTERSECT",VERTEX,{"derivedFrom":[subQ0,sQuery(id+"F0.wireOp",EDGE,"E34.MirrorCS")]}),-1.0]])],"derivedFrom":subQ0})])],"isStart":false});}
            var Q9;
            {var subQ0=sQuery(id+"F0.wireOp",EDGE,"E26");Q9=makeQuery(id+"F2.opExtrude","CAP_EDGE",EDGE,{"disambiguationData":[OSD([subQ0]),TDD([makeQuery(id+"F0.imprint","IMPRINT",EDGE,{"disambiguationData":[TD([[makeQuery(id+"F0.imprint","INTERSECT",VERTEX,{"derivedFrom":[subQ0,sQuery(id+"F0.wireOp",EDGE,"E31.0")]}),-1.0]])],"derivedFrom":subQ0})])],"isStart":false});}
            var Q10;
            {var subQ0=sQuery(id+"F0.wireOp",EDGE,"E34.MirrorCS");Q10=makeQuery(id+"F2.opExtrude","CAP_EDGE",EDGE,{"disambiguationData":[OSD([subQ0]),TDD([makeQuery(id+"F0.imprint","IMPRINT",EDGE,{"disambiguationData":[TD([[makeQuery(id+"F0.imprint","INTERSECT",VERTEX,{"derivedFrom":[sQuery(id+"F0.wireOp",EDGE,"E31.0"),subQ0]}),-1.0]])],"derivedFrom":subQ0})])],"isStart":false});}
            var Q11;
            {var subQ0=sQuery(id+"F0.wireOp",EDGE,"E33.0");Q11=makeQuery(id+"F2.opExtrude","CAP_EDGE",EDGE,{"disambiguationData":[OSD([subQ0]),TDD([makeQuery(id+"F0.imprint","IMPRINT",EDGE,{"disambiguationData":[TD([[makeQuery(id+"F0.imprint","INTERSECT",VERTEX,{"derivedFrom":[subQ0,sQuery(id+"F0.wireOp",EDGE,"E36.MirrorCS")]}),-1.0]])],"derivedFrom":subQ0})])],"isStart":false});}
            var Q12;
            {var subQ0=sQuery(id+"F0.wireOp",EDGE,"E36.MirrorCS");Q12=makeQuery(id+"F2.opExtrude","CAP_EDGE",EDGE,{"disambiguationData":[OSD([subQ0]),TDD([makeQuery(id+"F0.imprint","IMPRINT",EDGE,{"disambiguationData":[TD([[makeQuery(id+"F0.imprint","INTERSECT",VERTEX,{"derivedFrom":[sQuery(id+"F0.wireOp",EDGE,"E33.0"),subQ0]}),-1.0]])],"derivedFrom":subQ0})])],"isStart":false});}
            var Q13;
            {var subQ0=sQuery(id+"F0.wireOp",EDGE,"E35.0");Q13=makeQuery(id+"F2.opExtrude","CAP_EDGE",EDGE,{"disambiguationData":[OSD([subQ0]),TDD([makeQuery(id+"F0.imprint","IMPRINT",EDGE,{"disambiguationData":[TD([[makeQuery(id+"F0.imprint","INTERSECT",VERTEX,{"derivedFrom":[subQ0,sQuery(id+"F0.wireOp",EDGE,"E38.0")]}),-1.0]])],"derivedFrom":subQ0})])],"isStart":false});}
            var Q14;
            {var subQ0=sQuery(id+"F0.wireOp",EDGE,"E38.0");Q14=makeQuery(id+"F2.opExtrude","CAP_EDGE",EDGE,{"disambiguationData":[OSD([subQ0]),TDD([makeQuery(id+"F0.imprint","IMPRINT",EDGE,{"disambiguationData":[TD([[makeQuery(id+"F0.imprint","INTERSECT",VERTEX,{"derivedFrom":[sQuery(id+"F0.wireOp",EDGE,"E35.0"),subQ0]}),-1.0]])],"derivedFrom":subQ0})])],"isStart":false});}
            var Q15;
            {var subQ0=sQuery(id+"F0.wireOp",EDGE,"E37.0");Q15=makeQuery(id+"F2.opExtrude","CAP_EDGE",EDGE,{"disambiguationData":[OSD([subQ0]),TDD([makeQuery(id+"F0.imprint","IMPRINT",EDGE,{"disambiguationData":[TD([[makeQuery(id+"F0.imprint","INTERSECT",VERTEX,{"derivedFrom":[subQ0,sQuery(id+"F0.wireOp",EDGE,"E40.0")]}),-1.0]])],"derivedFrom":subQ0})])],"isStart":false});}
            var Q16;
            {var subQ0=sQuery(id+"F0.wireOp",EDGE,"E40.0");Q16=makeQuery(id+"F2.opExtrude","CAP_EDGE",EDGE,{"disambiguationData":[OSD([subQ0]),TDD([makeQuery(id+"F0.imprint","IMPRINT",EDGE,{"disambiguationData":[TD([[makeQuery(id+"F0.imprint","INTERSECT",VERTEX,{"derivedFrom":[sQuery(id+"F0.wireOp",EDGE,"E37.0"),subQ0]}),-1.0]])],"derivedFrom":subQ0})])],"isStart":false});}
            var Q17;
            {var subQ0=sQuery(id+"F0.wireOp",EDGE,"E39.0");Q17=makeQuery(id+"F2.opExtrude","CAP_EDGE",EDGE,{"disambiguationData":[OSD([subQ0]),TDD([makeQuery(id+"F0.imprint","IMPRINT",EDGE,{"disambiguationData":[TD([[makeQuery(id+"F0.imprint","INTERSECT",VERTEX,{"derivedFrom":[subQ0,sQuery(id+"F0.wireOp",EDGE,"E44.0")]}),-1.0]])],"derivedFrom":subQ0})])],"isStart":false});}
            var Q18;
            {var subQ0=sQuery(id+"F0.wireOp",EDGE,"E44.0");Q18=makeQuery(id+"F2.opExtrude","CAP_EDGE",EDGE,{"disambiguationData":[OSD([subQ0]),TDD([makeQuery(id+"F0.imprint","IMPRINT",EDGE,{"disambiguationData":[TD([[makeQuery(id+"F0.imprint","INTERSECT",VERTEX,{"derivedFrom":[sQuery(id+"F0.wireOp",EDGE,"E39.0"),subQ0]}),-1.0]])],"derivedFrom":subQ0})])],"isStart":false});}
            var Q19;
            {var subQ0=sQuery(id+"F0.wireOp",EDGE,"E43.0");Q19=makeQuery(id+"F2.opExtrude","CAP_EDGE",EDGE,{"disambiguationData":[OSD([subQ0]),TDD([makeQuery(id+"F0.imprint","IMPRINT",EDGE,{"disambiguationData":[TD([[makeQuery(id+"F0.imprint","INTERSECT",VERTEX,{"derivedFrom":[sQuery(id+"F0.wireOp",EDGE,"E42.0"),subQ0]}),-1.0]])],"derivedFrom":subQ0})])],"isStart":false});}
            var Q20;
            {var subQ0=sQuery(id+"F0.wireOp",EDGE,"E42.0");Q20=makeQuery(id+"F2.opExtrude","CAP_EDGE",EDGE,{"disambiguationData":[OSD([subQ0]),TDD([makeQuery(id+"F0.imprint","IMPRINT",EDGE,{"disambiguationData":[TD([[makeQuery(id+"F0.imprint","INTERSECT",VERTEX,{"derivedFrom":[subQ0,sQuery(id+"F0.wireOp",EDGE,"E43.0")]}),-1.0]])],"derivedFrom":subQ0})])],"isStart":false});}
            var Q21;
            {var subQ0=sQuery(id+"F0.wireOp",EDGE,"E41.0");Q21=makeQuery(id+"F2.opExtrude","CAP_EDGE",EDGE,{"disambiguationData":[OSD([subQ0]),TDD([makeQuery(id+"F0.imprint","IMPRINT",EDGE,{"disambiguationData":[TD([[makeQuery(id+"F0.imprint","INTERSECT",VERTEX,{"derivedFrom":[sQuery(id+"F0.wireOp",EDGE,"E30.8.0"),subQ0]}),-1.0]])],"derivedFrom":subQ0})])],"isStart":false});}
            var Q22;
            {var subQ0=sQuery(id+"F0.wireOp",EDGE,"E27");Q22=makeQuery(id+"F2.opExtrude","CAP_EDGE",EDGE,{"disambiguationData":[OSD([subQ0]),TDD([makeQuery(id+"F0.imprint","IMPRINT",EDGE,{"disambiguationData":[TD([[makeQuery(id+"F0.imprint","INTERSECT",VERTEX,{"derivedFrom":[subQ0,sQuery(id+"F0.wireOp",EDGE,"E30.8.0")]}),1.0]])],"derivedFrom":subQ0})])],"isStart":false});}
            var Q23;
            {var subQ0=sQuery(id+"F0.wireOp",EDGE,"E26");Q23=makeQuery(id+"F2.opExtrude","CAP_EDGE",EDGE,{"disambiguationData":[OSD([subQ0]),TDD([makeQuery(id+"F0.imprint","IMPRINT",EDGE,{"disambiguationData":[TD([[makeQuery(id+"F0.imprint","INTERSECT",VERTEX,{"derivedFrom":[subQ0,sQuery(id+"F0.wireOp",EDGE,"E43.0")]}),-1.0]])],"derivedFrom":subQ0})])],"isStart":false});}
            var Q24;
            {var subQ0=sQuery(id+"F0.wireOp",EDGE,"E27");Q24=makeQuery(id+"F2.opExtrude","CAP_EDGE",EDGE,{"disambiguationData":[OSD([subQ0]),TDD([makeQuery(id+"F0.imprint","IMPRINT",EDGE,{"disambiguationData":[TD([[makeQuery(id+"F0.imprint","INTERSECT",VERTEX,{"derivedFrom":[subQ0,sQuery(id+"F0.wireOp",EDGE,"E43.0")]}),-1.0]])],"derivedFrom":subQ0})])],"isStart":false});}
            var Q25;
            {var subQ0=sQuery(id+"F0.wireOp",EDGE,"E27");Q25=makeQuery(id+"F2.opExtrude","CAP_EDGE",EDGE,{"disambiguationData":[OSD([subQ0]),TDD([makeQuery(id+"F0.imprint","IMPRINT",EDGE,{"disambiguationData":[TD([[makeQuery(id+"F0.imprint","INTERSECT",VERTEX,{"derivedFrom":[subQ0,sQuery(id+"F0.wireOp",EDGE,"E39.0")]}),-1.0]])],"derivedFrom":subQ0})])],"isStart":false});}
            var Q26;
            {var subQ0=sQuery(id+"F0.wireOp",EDGE,"E26");Q26=makeQuery(id+"F2.opExtrude","CAP_EDGE",EDGE,{"disambiguationData":[OSD([subQ0]),TDD([makeQuery(id+"F0.imprint","IMPRINT",EDGE,{"disambiguationData":[TD([[makeQuery(id+"F0.imprint","INTERSECT",VERTEX,{"derivedFrom":[subQ0,sQuery(id+"F0.wireOp",EDGE,"E39.0")]}),-1.0]])],"derivedFrom":subQ0})])],"isStart":false});}
            var Q27;
            {var subQ0=sQuery(id+"F0.wireOp",EDGE,"E26");Q27=makeQuery(id+"F2.opExtrude","CAP_EDGE",EDGE,{"disambiguationData":[OSD([subQ0]),TDD([makeQuery(id+"F0.imprint","IMPRINT",EDGE,{"disambiguationData":[TD([[makeQuery(id+"F0.imprint","INTERSECT",VERTEX,{"derivedFrom":[subQ0,sQuery(id+"F0.wireOp",EDGE,"E37.0")]}),-1.0]])],"derivedFrom":subQ0})])],"isStart":false});}
            var Q28;
            {var subQ0=sQuery(id+"F0.wireOp",EDGE,"E27");Q28=makeQuery(id+"F2.opExtrude","CAP_EDGE",EDGE,{"disambiguationData":[OSD([subQ0]),TDD([makeQuery(id+"F0.imprint","IMPRINT",EDGE,{"disambiguationData":[TD([[makeQuery(id+"F0.imprint","INTERSECT",VERTEX,{"derivedFrom":[subQ0,sQuery(id+"F0.wireOp",EDGE,"E37.0")]}),-1.0]])],"derivedFrom":subQ0})])],"isStart":false});}
            var Q29;
            {var subQ0=sQuery(id+"F0.wireOp",EDGE,"E26");Q29=makeQuery(id+"F2.opExtrude","CAP_EDGE",EDGE,{"disambiguationData":[OSD([subQ0]),TDD([makeQuery(id+"F0.imprint","IMPRINT",EDGE,{"disambiguationData":[TD([[makeQuery(id+"F0.imprint","INTERSECT",VERTEX,{"derivedFrom":[subQ0,sQuery(id+"F0.wireOp",EDGE,"E35.0")]}),-1.0]])],"derivedFrom":subQ0})])],"isStart":false});}
            var Q30;
            {var subQ0=sQuery(id+"F0.wireOp",EDGE,"E27");Q30=makeQuery(id+"F2.opExtrude","CAP_EDGE",EDGE,{"disambiguationData":[OSD([subQ0]),TDD([makeQuery(id+"F0.imprint","IMPRINT",EDGE,{"disambiguationData":[TD([[makeQuery(id+"F0.imprint","INTERSECT",VERTEX,{"derivedFrom":[subQ0,sQuery(id+"F0.wireOp",EDGE,"E35.0")]}),-1.0]])],"derivedFrom":subQ0})])],"isStart":false});}
            var Q31;
            {var subQ0=sQuery(id+"F0.wireOp",EDGE,"E27");Q31=makeQuery(id+"F2.opExtrude","CAP_EDGE",EDGE,{"disambiguationData":[OSD([subQ0]),TDD([makeQuery(id+"F0.imprint","IMPRINT",EDGE,{"disambiguationData":[TD([[makeQuery(id+"F0.imprint","INTERSECT",VERTEX,{"derivedFrom":[subQ0,sQuery(id+"F0.wireOp",EDGE,"E33.0")]}),-1.0]])],"derivedFrom":subQ0})])],"isStart":false});}
            var Q32;
            {var subQ0=sQuery(id+"F0.wireOp",EDGE,"E26");Q32=makeQuery(id+"F2.opExtrude","CAP_EDGE",EDGE,{"disambiguationData":[OSD([subQ0]),TDD([makeQuery(id+"F0.imprint","IMPRINT",EDGE,{"disambiguationData":[TD([[makeQuery(id+"F0.imprint","INTERSECT",VERTEX,{"derivedFrom":[subQ0,sQuery(id+"F0.wireOp",EDGE,"E33.0")]}),-1.0]])],"derivedFrom":subQ0})])],"isStart":false});}
            var Q33;
            {var subQ0=sQuery(id+"F0.wireOp",EDGE,"E26");Q33=makeQuery(id+"F2.opExtrude","CAP_EDGE",EDGE,{"disambiguationData":[OSD([subQ0]),TDD([makeQuery(id+"F0.imprint","IMPRINT",EDGE,{"disambiguationData":[TD([[makeQuery(id+"F0.imprint","INTERSECT",VERTEX,{"derivedFrom":[subQ0,sQuery(id+"F0.wireOp",EDGE,"E30.8.0")]}),1.0]])],"derivedFrom":subQ0})])],"isStart":false});}
            var Q34;
            {var subQ0=sQuery(id+"F0.wireOp",EDGE,"E41.0");Q34=makeQuery(id+"F2.opExtrude","CAP_EDGE",EDGE,{"disambiguationData":[OSD([subQ0]),TDD([makeQuery(id+"F0.imprint","IMPRINT",EDGE,{"disambiguationData":[TD([[makeQuery(id+"F0.imprint","INTERSECT",VERTEX,{"derivedFrom":[sQuery(id+"F0.wireOp",EDGE,"E25"),subQ0]}),1.0]])],"derivedFrom":subQ0})])],"isStart":false});}
            var Q35;
            {var subQ0=sQuery(id+"F0.wireOp",EDGE,"E42.0");Q35=makeQuery(id+"F2.opExtrude","CAP_EDGE",EDGE,{"disambiguationData":[OSD([subQ0]),TDD([makeQuery(id+"F0.imprint","IMPRINT",EDGE,{"disambiguationData":[TD([[makeQuery(id+"F0.imprint","INTERSECT",VERTEX,{"derivedFrom":[sQuery(id+"F0.wireOp",EDGE,"E25"),subQ0]}),1.0]])],"derivedFrom":subQ0})])],"isStart":false});}
            var Q36;
            {var subQ0=sQuery(id+"F0.wireOp",EDGE,"E43.0");Q36=makeQuery(id+"F2.opExtrude","CAP_EDGE",EDGE,{"disambiguationData":[OSD([subQ0]),TDD([makeQuery(id+"F0.imprint","IMPRINT",EDGE,{"disambiguationData":[TD([[makeQuery(id+"F0.imprint","INTERSECT",VERTEX,{"derivedFrom":[sQuery(id+"F0.wireOp",EDGE,"E25"),subQ0]}),1.0]])],"derivedFrom":subQ0})])],"isStart":false});}
            var Q37;
            {var subQ0=sQuery(id+"F0.wireOp",EDGE,"E44.0");Q37=makeQuery(id+"F2.opExtrude","CAP_EDGE",EDGE,{"disambiguationData":[OSD([subQ0]),TDD([makeQuery(id+"F0.imprint","IMPRINT",EDGE,{"disambiguationData":[TD([[makeQuery(id+"F0.imprint","INTERSECT",VERTEX,{"derivedFrom":[sQuery(id+"F0.wireOp",EDGE,"E25"),subQ0]}),1.0]])],"derivedFrom":subQ0})])],"isStart":false});}
            var Q38;
            {var subQ0=sQuery(id+"F0.wireOp",EDGE,"E39.0");Q38=makeQuery(id+"F2.opExtrude","CAP_EDGE",EDGE,{"disambiguationData":[OSD([subQ0]),TDD([makeQuery(id+"F0.imprint","IMPRINT",EDGE,{"disambiguationData":[TD([[makeQuery(id+"F0.imprint","INTERSECT",VERTEX,{"derivedFrom":[sQuery(id+"F0.wireOp",EDGE,"E25"),subQ0]}),1.0]])],"derivedFrom":subQ0})])],"isStart":false});}
            var Q39;
            {var subQ0=sQuery(id+"F0.wireOp",EDGE,"E40.0");Q39=makeQuery(id+"F2.opExtrude","CAP_EDGE",EDGE,{"disambiguationData":[OSD([subQ0]),TDD([makeQuery(id+"F0.imprint","IMPRINT",EDGE,{"disambiguationData":[TD([[makeQuery(id+"F0.imprint","INTERSECT",VERTEX,{"derivedFrom":[sQuery(id+"F0.wireOp",EDGE,"E25"),subQ0]}),1.0]])],"derivedFrom":subQ0})])],"isStart":false});}
            var Q40;
            {var subQ0=sQuery(id+"F0.wireOp",EDGE,"E38.0");Q40=makeQuery(id+"F2.opExtrude","CAP_EDGE",EDGE,{"disambiguationData":[OSD([subQ0]),TDD([makeQuery(id+"F0.imprint","IMPRINT",EDGE,{"disambiguationData":[TD([[makeQuery(id+"F0.imprint","INTERSECT",VERTEX,{"derivedFrom":[sQuery(id+"F0.wireOp",EDGE,"E25"),subQ0]}),1.0]])],"derivedFrom":subQ0})])],"isStart":false});}
            var Q41;
            {var subQ0=sQuery(id+"F0.wireOp",EDGE,"E35.0");Q41=makeQuery(id+"F2.opExtrude","CAP_EDGE",EDGE,{"disambiguationData":[OSD([subQ0]),TDD([makeQuery(id+"F0.imprint","IMPRINT",EDGE,{"disambiguationData":[TD([[makeQuery(id+"F0.imprint","INTERSECT",VERTEX,{"derivedFrom":[sQuery(id+"F0.wireOp",EDGE,"E25"),subQ0]}),1.0]])],"derivedFrom":subQ0})])],"isStart":false});}
            var Q42;
            {var subQ0=sQuery(id+"F0.wireOp",EDGE,"E36.MirrorCS");Q42=makeQuery(id+"F2.opExtrude","CAP_EDGE",EDGE,{"disambiguationData":[OSD([subQ0]),TDD([makeQuery(id+"F0.imprint","IMPRINT",EDGE,{"disambiguationData":[TD([[makeQuery(id+"F0.imprint","INTERSECT",VERTEX,{"derivedFrom":[sQuery(id+"F0.wireOp",EDGE,"E25"),subQ0]}),1.0]])],"derivedFrom":subQ0})])],"isStart":false});}
            var Q43;
            {var subQ0=sQuery(id+"F0.wireOp",EDGE,"E33.0");Q43=makeQuery(id+"F2.opExtrude","CAP_EDGE",EDGE,{"disambiguationData":[OSD([subQ0]),TDD([makeQuery(id+"F0.imprint","IMPRINT",EDGE,{"disambiguationData":[TD([[makeQuery(id+"F0.imprint","INTERSECT",VERTEX,{"derivedFrom":[sQuery(id+"F0.wireOp",EDGE,"E25"),subQ0]}),1.0]])],"derivedFrom":subQ0})])],"isStart":false});}
            var Q44;
            {var subQ0=sQuery(id+"F0.wireOp",EDGE,"E34.MirrorCS");Q44=makeQuery(id+"F2.opExtrude","CAP_EDGE",EDGE,{"disambiguationData":[OSD([subQ0]),TDD([makeQuery(id+"F0.imprint","IMPRINT",EDGE,{"disambiguationData":[TD([[makeQuery(id+"F0.imprint","INTERSECT",VERTEX,{"derivedFrom":[sQuery(id+"F0.wireOp",EDGE,"E25"),subQ0]}),1.0]])],"derivedFrom":subQ0})])],"isStart":false});}
            var Q45;
            {var subQ0=sQuery(id+"F0.wireOp",EDGE,"E25");Q45=makeQuery(id+"F2.opExtrude","CAP_EDGE",EDGE,{"disambiguationData":[OSD([subQ0]),TDD([makeQuery(id+"F0.imprint","IMPRINT",EDGE,{"disambiguationData":[TD([[makeQuery(id+"F0.imprint","INTERSECT",VERTEX,{"derivedFrom":[subQ0,sQuery(id+"F0.wireOp",EDGE,"E31.0")]}),-1.0]])],"derivedFrom":subQ0})])],"isStart":false});}
            var Q46;
            {var subQ0=sQuery(id+"F0.wireOp",EDGE,"E24");Q46=makeQuery(id+"F2.opExtrude","CAP_EDGE",EDGE,{"disambiguationData":[OSD([subQ0]),TDD([makeQuery(id+"F0.imprint","IMPRINT",EDGE,{"disambiguationData":[TD([[makeQuery(id+"F0.imprint","INTERSECT",VERTEX,{"derivedFrom":[subQ0,sQuery(id+"F0.wireOp",EDGE,"E31.0")]}),-1.0]])],"derivedFrom":subQ0})])],"isStart":false});}
            var Q47;
            {var subQ0=sQuery(id+"F0.wireOp",EDGE,"E25");Q47=makeQuery(id+"F2.opExtrude","CAP_EDGE",EDGE,{"disambiguationData":[OSD([subQ0]),TDD([makeQuery(id+"F0.imprint","IMPRINT",EDGE,{"disambiguationData":[TD([[makeQuery(id+"F0.imprint","INTERSECT",VERTEX,{"derivedFrom":[subQ0,sQuery(id+"F0.wireOp",EDGE,"E33.0")]}),-1.0]])],"derivedFrom":subQ0})])],"isStart":false});}
            var Q48;
            {var subQ0=sQuery(id+"F0.wireOp",EDGE,"E24");Q48=makeQuery(id+"F2.opExtrude","CAP_EDGE",EDGE,{"disambiguationData":[OSD([subQ0]),TDD([makeQuery(id+"F0.imprint","IMPRINT",EDGE,{"disambiguationData":[TD([[makeQuery(id+"F0.imprint","INTERSECT",VERTEX,{"derivedFrom":[subQ0,sQuery(id+"F0.wireOp",EDGE,"E33.0")]}),-1.0]])],"derivedFrom":subQ0})])],"isStart":false});}
            var Q49;
            {var subQ0=sQuery(id+"F0.wireOp",EDGE,"E25");Q49=makeQuery(id+"F2.opExtrude","CAP_EDGE",EDGE,{"disambiguationData":[OSD([subQ0]),TDD([makeQuery(id+"F0.imprint","IMPRINT",EDGE,{"disambiguationData":[TD([[makeQuery(id+"F0.imprint","INTERSECT",VERTEX,{"derivedFrom":[subQ0,sQuery(id+"F0.wireOp",EDGE,"E35.0")]}),-1.0]])],"derivedFrom":subQ0})])],"isStart":false});}
            var Q50;
            {var subQ0=sQuery(id+"F0.wireOp",EDGE,"E24");Q50=makeQuery(id+"F2.opExtrude","CAP_EDGE",EDGE,{"disambiguationData":[OSD([subQ0]),TDD([makeQuery(id+"F0.imprint","IMPRINT",EDGE,{"disambiguationData":[TD([[makeQuery(id+"F0.imprint","INTERSECT",VERTEX,{"derivedFrom":[subQ0,sQuery(id+"F0.wireOp",EDGE,"E35.0")]}),-1.0]])],"derivedFrom":subQ0})])],"isStart":false});}
            var Q51;
            {var subQ0=sQuery(id+"F0.wireOp",EDGE,"E25");Q51=makeQuery(id+"F2.opExtrude","CAP_EDGE",EDGE,{"disambiguationData":[OSD([subQ0]),TDD([makeQuery(id+"F0.imprint","IMPRINT",EDGE,{"disambiguationData":[TD([[makeQuery(id+"F0.imprint","INTERSECT",VERTEX,{"derivedFrom":[subQ0,sQuery(id+"F0.wireOp",EDGE,"E37.0")]}),-1.0]])],"derivedFrom":subQ0})])],"isStart":false});}
            var Q52;
            {var subQ0=sQuery(id+"F0.wireOp",EDGE,"E24");Q52=makeQuery(id+"F2.opExtrude","CAP_EDGE",EDGE,{"disambiguationData":[OSD([subQ0]),TDD([makeQuery(id+"F0.imprint","IMPRINT",EDGE,{"disambiguationData":[TD([[makeQuery(id+"F0.imprint","INTERSECT",VERTEX,{"derivedFrom":[subQ0,sQuery(id+"F0.wireOp",EDGE,"E37.0")]}),-1.0]])],"derivedFrom":subQ0})])],"isStart":false});}
            var Q53;
            {var subQ0=sQuery(id+"F0.wireOp",EDGE,"E25");Q53=makeQuery(id+"F2.opExtrude","CAP_EDGE",EDGE,{"disambiguationData":[OSD([subQ0]),TDD([makeQuery(id+"F0.imprint","IMPRINT",EDGE,{"disambiguationData":[TD([[makeQuery(id+"F0.imprint","INTERSECT",VERTEX,{"derivedFrom":[subQ0,sQuery(id+"F0.wireOp",EDGE,"E39.0")]}),-1.0]])],"derivedFrom":subQ0})])],"isStart":false});}
            var Q54;
            {var subQ0=sQuery(id+"F0.wireOp",EDGE,"E24");Q54=makeQuery(id+"F2.opExtrude","CAP_EDGE",EDGE,{"disambiguationData":[OSD([subQ0]),TDD([makeQuery(id+"F0.imprint","IMPRINT",EDGE,{"disambiguationData":[TD([[makeQuery(id+"F0.imprint","INTERSECT",VERTEX,{"derivedFrom":[subQ0,sQuery(id+"F0.wireOp",EDGE,"E39.0")]}),-1.0]])],"derivedFrom":subQ0})])],"isStart":false});}
            var Q55;
            {var subQ0=sQuery(id+"F0.wireOp",EDGE,"E25");Q55=makeQuery(id+"F2.opExtrude","CAP_EDGE",EDGE,{"disambiguationData":[OSD([subQ0]),TDD([makeQuery(id+"F0.imprint","IMPRINT",EDGE,{"disambiguationData":[TD([[makeQuery(id+"F0.imprint","INTERSECT",VERTEX,{"derivedFrom":[subQ0,sQuery(id+"F0.wireOp",EDGE,"E43.0")]}),-1.0]])],"derivedFrom":subQ0})])],"isStart":false});}
            var Q56;
            {var subQ0=sQuery(id+"F0.wireOp",EDGE,"E24");Q56=makeQuery(id+"F2.opExtrude","CAP_EDGE",EDGE,{"disambiguationData":[OSD([subQ0]),TDD([makeQuery(id+"F0.imprint","IMPRINT",EDGE,{"disambiguationData":[TD([[makeQuery(id+"F0.imprint","INTERSECT",VERTEX,{"derivedFrom":[subQ0,sQuery(id+"F0.wireOp",EDGE,"E43.0")]}),-1.0]])],"derivedFrom":subQ0})])],"isStart":false});}
            var Q57;
            {var subQ0=sQuery(id+"F0.wireOp",EDGE,"E24");Q57=makeQuery(id+"F2.opExtrude","CAP_EDGE",EDGE,{"disambiguationData":[OSD([subQ0]),TDD([makeQuery(id+"F0.imprint","IMPRINT",EDGE,{"disambiguationData":[TD([[makeQuery(id+"F0.imprint","INTERSECT",VERTEX,{"derivedFrom":[subQ0,sQuery(id+"F0.wireOp",EDGE,"E30.8.0")]}),1.0]])],"derivedFrom":subQ0})])],"isStart":false});}
            var Q58;
            {var subQ0=sQuery(id+"F0.wireOp",EDGE,"E41.0");Q58=makeQuery(id+"F2.opExtrude","CAP_EDGE",EDGE,{"disambiguationData":[OSD([subQ0]),TDD([makeQuery(id+"F0.imprint","IMPRINT",EDGE,{"disambiguationData":[TD([[makeQuery(id+"F0.imprint","INTERSECT",VERTEX,{"derivedFrom":[sQuery(id+"F0.wireOp",EDGE,"E22"),subQ0]}),1.0]])],"derivedFrom":subQ0})])],"isStart":false});}
            var Q59;
            {var subQ0=sQuery(id+"F0.wireOp",EDGE,"E42.0");Q59=makeQuery(id+"F2.opExtrude","CAP_EDGE",EDGE,{"disambiguationData":[OSD([subQ0]),TDD([makeQuery(id+"F0.imprint","IMPRINT",EDGE,{"disambiguationData":[TD([[makeQuery(id+"F0.imprint","INTERSECT",VERTEX,{"derivedFrom":[sQuery(id+"F0.wireOp",EDGE,"E22"),subQ0]}),1.0]])],"derivedFrom":subQ0})])],"isStart":false});}
            var Q60;
            {var subQ0=sQuery(id+"F0.wireOp",EDGE,"E25");Q60=makeQuery(id+"F2.opExtrude","CAP_EDGE",EDGE,{"disambiguationData":[OSD([subQ0]),TDD([makeQuery(id+"F0.imprint","IMPRINT",EDGE,{"disambiguationData":[TD([[makeQuery(id+"F0.imprint","INTERSECT",VERTEX,{"derivedFrom":[subQ0,sQuery(id+"F0.wireOp",EDGE,"E30.8.0")]}),1.0]])],"derivedFrom":subQ0})])],"isStart":false});}
            var Q61;
            {var subQ0=sQuery(id+"F0.wireOp",EDGE,"E43.0");Q61=makeQuery(id+"F2.opExtrude","CAP_EDGE",EDGE,{"disambiguationData":[OSD([subQ0]),TDD([makeQuery(id+"F0.imprint","IMPRINT",EDGE,{"disambiguationData":[TD([[makeQuery(id+"F0.imprint","INTERSECT",VERTEX,{"derivedFrom":[sQuery(id+"F0.wireOp",EDGE,"E22"),subQ0]}),1.0]])],"derivedFrom":subQ0})])],"isStart":false});}
            var Q62;
            {var subQ0=sQuery(id+"F0.wireOp",EDGE,"E44.0");Q62=makeQuery(id+"F2.opExtrude","CAP_EDGE",EDGE,{"disambiguationData":[OSD([subQ0]),TDD([makeQuery(id+"F0.imprint","IMPRINT",EDGE,{"disambiguationData":[TD([[makeQuery(id+"F0.imprint","INTERSECT",VERTEX,{"derivedFrom":[sQuery(id+"F0.wireOp",EDGE,"E22"),subQ0]}),1.0]])],"derivedFrom":subQ0})])],"isStart":false});}
            var Q63;
            {var subQ0=sQuery(id+"F0.wireOp",EDGE,"E39.0");Q63=makeQuery(id+"F2.opExtrude","CAP_EDGE",EDGE,{"disambiguationData":[OSD([subQ0]),TDD([makeQuery(id+"F0.imprint","IMPRINT",EDGE,{"disambiguationData":[TD([[makeQuery(id+"F0.imprint","INTERSECT",VERTEX,{"derivedFrom":[sQuery(id+"F0.wireOp",EDGE,"E22"),subQ0]}),1.0]])],"derivedFrom":subQ0})])],"isStart":false});}
            var Q64;
            {var subQ0=sQuery(id+"F0.wireOp",EDGE,"E40.0");Q64=makeQuery(id+"F2.opExtrude","CAP_EDGE",EDGE,{"disambiguationData":[OSD([subQ0]),TDD([makeQuery(id+"F0.imprint","IMPRINT",EDGE,{"disambiguationData":[TD([[makeQuery(id+"F0.imprint","INTERSECT",VERTEX,{"derivedFrom":[sQuery(id+"F0.wireOp",EDGE,"E22"),subQ0]}),1.0]])],"derivedFrom":subQ0})])],"isStart":false});}
            var Q65;
            {var subQ0=sQuery(id+"F0.wireOp",EDGE,"E37.0");Q65=makeQuery(id+"F2.opExtrude","CAP_EDGE",EDGE,{"disambiguationData":[OSD([subQ0]),TDD([makeQuery(id+"F0.imprint","IMPRINT",EDGE,{"disambiguationData":[TD([[makeQuery(id+"F0.imprint","INTERSECT",VERTEX,{"derivedFrom":[sQuery(id+"F0.wireOp",EDGE,"E25"),subQ0]}),1.0]])],"derivedFrom":subQ0})])],"isStart":false});}
            var Q66;
            {var subQ0=sQuery(id+"F0.wireOp",EDGE,"E37.0");Q66=makeQuery(id+"F2.opExtrude","CAP_EDGE",EDGE,{"disambiguationData":[OSD([subQ0]),TDD([makeQuery(id+"F0.imprint","IMPRINT",EDGE,{"disambiguationData":[TD([[makeQuery(id+"F0.imprint","INTERSECT",VERTEX,{"derivedFrom":[sQuery(id+"F0.wireOp",EDGE,"E22"),subQ0]}),1.0]])],"derivedFrom":subQ0})])],"isStart":false});}
            var Q67;
            {var subQ0=sQuery(id+"F0.wireOp",EDGE,"E38.0");Q67=makeQuery(id+"F2.opExtrude","CAP_EDGE",EDGE,{"disambiguationData":[OSD([subQ0]),TDD([makeQuery(id+"F0.imprint","IMPRINT",EDGE,{"disambiguationData":[TD([[makeQuery(id+"F0.imprint","INTERSECT",VERTEX,{"derivedFrom":[sQuery(id+"F0.wireOp",EDGE,"E22"),subQ0]}),1.0]])],"derivedFrom":subQ0})])],"isStart":false});}
            var Q68;
            {var subQ0=sQuery(id+"F0.wireOp",EDGE,"E35.0");Q68=makeQuery(id+"F2.opExtrude","CAP_EDGE",EDGE,{"disambiguationData":[OSD([subQ0]),TDD([makeQuery(id+"F0.imprint","IMPRINT",EDGE,{"disambiguationData":[TD([[makeQuery(id+"F0.imprint","INTERSECT",VERTEX,{"derivedFrom":[sQuery(id+"F0.wireOp",EDGE,"E22"),subQ0]}),1.0]])],"derivedFrom":subQ0})])],"isStart":false});}
            var Q69;
            {var subQ0=sQuery(id+"F0.wireOp",EDGE,"E36.MirrorCS");Q69=makeQuery(id+"F2.opExtrude","CAP_EDGE",EDGE,{"disambiguationData":[OSD([subQ0]),TDD([makeQuery(id+"F0.imprint","IMPRINT",EDGE,{"disambiguationData":[TD([[makeQuery(id+"F0.imprint","INTERSECT",VERTEX,{"derivedFrom":[sQuery(id+"F0.wireOp",EDGE,"E22"),subQ0]}),1.0]])],"derivedFrom":subQ0})])],"isStart":false});}
            var Q70;
            {var subQ0=sQuery(id+"F0.wireOp",EDGE,"E33.0");Q70=makeQuery(id+"F2.opExtrude","CAP_EDGE",EDGE,{"disambiguationData":[OSD([subQ0]),TDD([makeQuery(id+"F0.imprint","IMPRINT",EDGE,{"disambiguationData":[TD([[makeQuery(id+"F0.imprint","INTERSECT",VERTEX,{"derivedFrom":[sQuery(id+"F0.wireOp",EDGE,"E22"),subQ0]}),1.0]])],"derivedFrom":subQ0})])],"isStart":false});}
            var Q71;
            {var subQ0=sQuery(id+"F0.wireOp",EDGE,"E34.MirrorCS");Q71=makeQuery(id+"F2.opExtrude","CAP_EDGE",EDGE,{"disambiguationData":[OSD([subQ0]),TDD([makeQuery(id+"F0.imprint","IMPRINT",EDGE,{"disambiguationData":[TD([[makeQuery(id+"F0.imprint","INTERSECT",VERTEX,{"derivedFrom":[sQuery(id+"F0.wireOp",EDGE,"E22"),subQ0]}),1.0]])],"derivedFrom":subQ0})])],"isStart":false});}
            var Q72;
            {var subQ0=sQuery(id+"F0.wireOp",EDGE,"E31.0");Q72=makeQuery(id+"F2.opExtrude","CAP_EDGE",EDGE,{"disambiguationData":[OSD([subQ0]),TDD([makeQuery(id+"F0.imprint","IMPRINT",EDGE,{"disambiguationData":[TD([[makeQuery(id+"F0.imprint","INTERSECT",VERTEX,{"derivedFrom":[sQuery(id+"F0.wireOp",EDGE,"E22"),subQ0]}),1.0]])],"derivedFrom":subQ0})])],"isStart":false});}
            var Q73;
            {var subQ0=sQuery(id+"F0.wireOp",EDGE,"E27");Q73=makeQuery(id+"F2.opExtrude","CAP_EDGE",EDGE,{"disambiguationData":[OSD([subQ0]),TDD([makeQuery(id+"F0.imprint","IMPRINT",EDGE,{"disambiguationData":[TD([[makeQuery(id+"F0.imprint","INTERSECT",VERTEX,{"derivedFrom":[subQ0,sQuery(id+"F0.wireOp",EDGE,"E29")]}),-1.0]])],"derivedFrom":subQ0})])],"isStart":false});}
            fillet(context, id + "F5", {"entities" : qUnion([Q0, Q1, Q2, Q3, Q4, Q5, Q6, Q7, Q8, Q9, Q10, Q11, Q12, Q13, Q14, Q15, Q16, Q17, Q18, Q19, Q20, Q21, Q22, Q23, Q24, Q25, Q26, Q27, Q28, Q29, Q30, Q31, Q32, Q33, Q34, Q35, Q36, Q37, Q38, Q39, Q40, Q41, Q42, Q43, Q44, Q45, Q46, Q47, Q48, Q49, Q50, Q51, Q52, Q53, Q54, Q55, Q56, Q57, Q58, Q59, Q60, Q61, Q62, Q63, Q64, Q65, Q66, Q67, Q68, Q69, Q70, Q71, Q72, Q73]), "radius" : 0.5 * mm, "tangentPropagation" : true, "allowEdgeOverflow" : false});
        }
        {
            var Q0;
            Q0=makeQuery(id+"F1.opExtrude","SWEPT_FACE",FACE,{"disambiguationData":[OSD([sQuery(id+"F0.wireOp",EDGE,"E4")])]});
            var sketch = newSketch(context, id + "F6", { "sketchPlane" : qUnion([Q0])});
            skLineSegment(sketch, "E45.0", {"start": v(-19.33, 1.5) * mm, "end": v(-19.33, 0) * mm});
            skArc(sketch, "E45.1", {"start": v(-20.33, 1.5) * mm, "mid": v(-19.83, 2) * mm, "end": v(-19.33, 1.5) * mm});
            skLineSegment(sketch, "E45.2", {"start": v(-20.33, 1.5) * mm, "end": v(-20.33, 0) * mm});
            skLineSegment(sketch, "E46", {"start": v(-20.33, 0) * mm, "end": v(-19.33, 0) * mm});
            skLineSegment(sketch, "E47.0", {"start": v(-40.67, 1.5) * mm, "end": v(-40.67, 0) * mm});
            skArc(sketch, "E47.1", {"start": v(-40.67, 1.5) * mm, "mid": v(-40.17, 2) * mm, "end": v(-39.67, 1.5) * mm});
            skLineSegment(sketch, "E47.2", {"start": v(-39.67, 1.5) * mm, "end": v(-39.67, 0) * mm});
            skLineSegment(sketch, "E48", {"start": v(-40.67, 0) * mm, "end": v(-39.67, 0) * mm});
            skSolve(sketch);
        }
        {
            var Q0;
            Q0 = qSketchRegion(id + "F6", true);
            var Q1;
            Q1=makeQuery(id+"F1.opExtrude","SWEPT_FACE",FACE,{"disambiguationData":[OSD([sQuery(id+"F0.wireOp",EDGE,"E8")])]});
            var Q2;
            Q2=makeQuery(id+"F1.opExtrude","SWEPT_FACE",FACE,{"disambiguationData":[OSD([sQuery(id+"F0.wireOp",EDGE,"E6")])]});
            extrude(context, id + "F7", {"entities" : qUnion([Q0]), "operationType" : NewBodyOperationType.ADD, "endBound" : BoundingType.UP_TO_SURFACE, "endBoundEntityFace" : qUnion([Q1]), "depth" : 25 * mm});
        }
        {
            var Q0;
            Q0=makeQuery(id+"F1.opExtrude","SWEPT_FACE",FACE,{"disambiguationData":[OSD([sQuery(id+"F0.wireOp",EDGE,"E6")])]});
            var sketch = newSketch(context, id + "F8", { "sketchPlane" : qUnion([Q0])});
            skLineSegment(sketch, "E49.0", {"start": v(40.67, 1.5) * mm, "end": v(40.67, 0) * mm});
            skArc(sketch, "E49.1", {"start": v(39.67, 1.5) * mm, "mid": v(40.17, 2) * mm, "end": v(40.67, 1.5) * mm});
            skLineSegment(sketch, "E49.2", {"start": v(39.67, 1.5) * mm, "end": v(39.67, 0) * mm});
            skLineSegment(sketch, "E50.0", {"start": v(19.33, 1.5) * mm, "end": v(19.33, 0) * mm});
            skArc(sketch, "E50.1", {"start": v(19.33, 1.5) * mm, "mid": v(19.83, 2) * mm, "end": v(20.33, 1.5) * mm});
            skLineSegment(sketch, "E50.2", {"start": v(20.33, 1.5) * mm, "end": v(20.33, 0) * mm});
            skLineSegment(sketch, "E51", {"start": v(19.33, 0) * mm, "end": v(20.33, 0) * mm});
            skLineSegment(sketch, "E52", {"start": v(39.67, 0) * mm, "end": v(40.67, 0) * mm});
            skSolve(sketch);
        }
        {
            var Q0;
            Q0 = qSketchRegion(id + "F8", true);
            extrude(context, id + "F9", {"entities" : qUnion([Q0]), "operationType" : NewBodyOperationType.ADD, "endBound" : BoundingType.UP_TO_NEXT, "depth" : 25 * mm});
        }
    });
